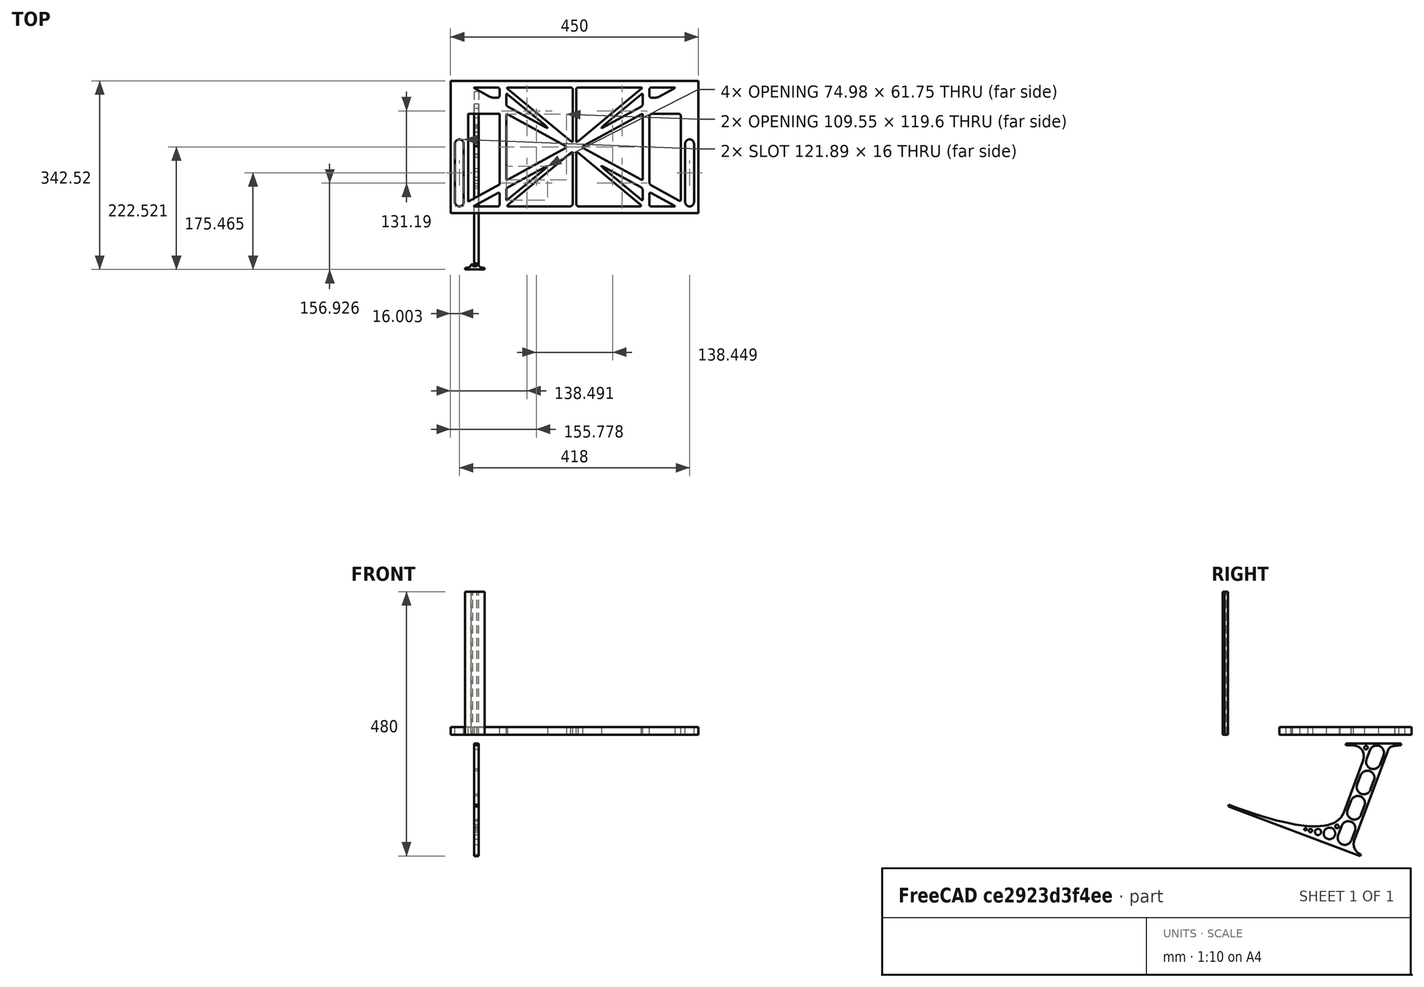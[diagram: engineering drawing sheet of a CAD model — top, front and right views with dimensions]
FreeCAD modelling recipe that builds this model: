
FCSTD DOCUMENT  (FreeCAD 0.19R0.19.2)
Label: laptopStand146FCStd
License: All rights reserved
LicenseURL: http://en.wikipedia.org/wiki/All_rights_reserved
objects: Sketcher::SketchObject×4, Part::Extrusion×3
note: 7 computed .brp shape members not serialized (recipe doc carries the construction recipe); baked Part::Feature solids carry a one-line shape summary decoded from their .brp

FEATURE [Sketcher::SketchObject] Sketch
  FullyConstrained = false
  sketch-geometry (349):
    g0: LineSegment StartX=-10.9272 StartY=-82.7794 StartZ=0 EndX=46.0728 EndY=-51.4823 EndZ=0
    g1: LineSegment StartX=-10.9272 StartY=76.4095 StartZ=0 EndX=-10.9272 EndY=-82.7794 EndZ=0
    g2: LineSegment StartX=46.0728 StartY=76.4095 StartZ=0 EndX=46.0728 EndY=-51.4823 EndZ=0
    g3: LineSegment StartX=-42.9272 StartY=136.221 StartZ=0 EndX=-42.9272 EndY=-103.779 EndZ=0
    g4: LineSegment StartX=407.073 StartY=136.221 StartZ=0 EndX=407.073 EndY=-103.779 EndZ=0
    g5: ArcOfCircle CenterX=-26.9272 CenterY=-83.7794 CenterZ=0 NormalX=0 NormalY=0 NormalZ=1 AngleXU=0 Radius=8 StartAngle=3.14159 EndAngle=6.28319
    g6: ArcOfCircle CenterX=391.073 CenterY=22.1087 CenterZ=0 NormalX=0 NormalY=0 NormalZ=1 AngleXU=0 Radius=8 StartAngle=-4.4e-15 EndAngle=3.14159
    g7: LineSegment StartX=399.073 StartY=22.1087 StartZ=0 EndX=399.073 EndY=-83.7794 EndZ=0
    g8: LineSegment StartX=383.073 StartY=22.1087 StartZ=0 EndX=383.073 EndY=-83.7794 EndZ=0
    g9: ArcOfCircle CenterX=391.073 CenterY=-83.7794 CenterZ=0 NormalX=0 NormalY=0 NormalZ=1 AngleXU=0 Radius=8 StartAngle=3.14159 EndAngle=6.28319
    g10: Circle CenterX=175.022 CenterY=27.0628 CenterZ=0 NormalX=0 NormalY=0 NormalZ=1 AngleXU=0 Radius=1
    g11: Circle CenterX=179.022 CenterY=24.8665 CenterZ=0 NormalX=0 NormalY=0 NormalZ=1 AngleXU=0 Radius=1
    g12: Circle CenterX=179.022 CenterY=27.0628 CenterZ=0 NormalX=0 NormalY=0 NormalZ=1 AngleXU=0 Radius=1
    g13: BSplineCurve PolesCount=3 KnotsCount=2 Degree=2 IsPeriodic=0
    g14: GeomPoint X=175.022 Y=27.0628 Z=0
    g15: GeomPoint X=179.022 Y=27.0628 Z=0
    g16: Circle CenterX=189.124 CenterY=27.0628 CenterZ=0 NormalX=0 NormalY=0 NormalZ=1 AngleXU=0 Radius=1
    g17: Circle CenterX=185.124 CenterY=24.8665 CenterZ=0 NormalX=0 NormalY=0 NormalZ=1 AngleXU=0 Radius=1
    g18: Circle CenterX=185.124 CenterY=27.0628 CenterZ=0 NormalX=0 NormalY=0 NormalZ=1 AngleXU=0 Radius=1
    g19: BSplineCurve PolesCount=3 KnotsCount=2 Degree=2 IsPeriodic=0
    g20: GeomPoint X=189.124 Y=27.0628 Z=0
    g21: GeomPoint X=185.124 Y=27.0628 Z=0
    g22: Circle CenterX=175.022 CenterY=5.37834 CenterZ=0 NormalX=0 NormalY=0 NormalZ=1 AngleXU=0 Radius=1
    g23: Circle CenterX=179.022 CenterY=7.57463 CenterZ=0 NormalX=0 NormalY=0 NormalZ=1 AngleXU=0 Radius=1
    g24: Circle CenterX=179.022 CenterY=5.34704 CenterZ=0 NormalX=0 NormalY=0 NormalZ=1 AngleXU=0 Radius=1
    g25: BSplineCurve PolesCount=3 KnotsCount=2 Degree=2 IsPeriodic=0
    g26: GeomPoint X=175.022 Y=5.37834 Z=0
    g27: GeomPoint X=179.022 Y=5.34704 Z=0
    g28: Circle CenterX=189.124 CenterY=5.37834 CenterZ=0 NormalX=0 NormalY=0 NormalZ=1 AngleXU=0 Radius=1
    g29: Circle CenterX=185.124 CenterY=7.57463 CenterZ=0 NormalX=0 NormalY=0 NormalZ=1 AngleXU=0 Radius=1
    g30: Circle CenterX=185.124 CenterY=5.34704 CenterZ=0 NormalX=0 NormalY=0 NormalZ=1 AngleXU=0 Radius=1
    g31: BSplineCurve PolesCount=3 KnotsCount=2 Degree=2 IsPeriodic=0
    g32: GeomPoint X=189.124 Y=5.37834 Z=0
    g33: GeomPoint X=185.124 Y=5.34704 Z=0
    g34: Circle CenterX=165.871 CenterY=18.1458 CenterZ=0 NormalX=0 NormalY=0 NormalZ=1 AngleXU=0 Radius=1
    g35: Circle CenterX=169.377 CenterY=16.2206 CenterZ=0 NormalX=0 NormalY=0 NormalZ=1 AngleXU=0 Radius=1
    g36: Circle CenterX=165.871 CenterY=14.2954 CenterZ=0 NormalX=0 NormalY=0 NormalZ=1 AngleXU=0 Radius=1
    g37: BSplineCurve PolesCount=3 KnotsCount=2 Degree=2 IsPeriodic=0
    g38: GeomPoint X=165.871 Y=18.1458 Z=0
    g39: GeomPoint X=165.871 Y=14.2954 Z=0
    g40: Circle CenterX=198.275 CenterY=18.1458 CenterZ=0 NormalX=0 NormalY=0 NormalZ=1 AngleXU=0 Radius=1
    g41: Circle CenterX=194.768 CenterY=16.2206 CenterZ=0 NormalX=0 NormalY=0 NormalZ=1 AngleXU=0 Radius=1
    g42: Circle CenterX=198.275 CenterY=14.2954 CenterZ=0 NormalX=0 NormalY=0 NormalZ=1 AngleXU=0 Radius=1
    g43: BSplineCurve PolesCount=3 KnotsCount=2 Degree=2 IsPeriodic=0
    g44: GeomPoint X=198.275 Y=18.1458 Z=0
    g45: GeomPoint X=198.275 Y=14.2954 Z=0
    g46: LineSegment StartX=407.073 StartY=-103.779 StartZ=0 EndX=-42.9272 EndY=-103.779 EndZ=0
    g47: LineSegment StartX=407.073 StartY=136.221 StartZ=0 EndX=-42.9272 EndY=136.221 EndZ=0
    g48: LineSegment StartX=46.0728 StartY=76.4095 StartZ=0 EndX=-10.9272 EndY=76.4095 EndZ=0
    g49: Circle CenterX=125.607 CenterY=54.1951 CenterZ=0 NormalX=0 NormalY=0 NormalZ=1 AngleXU=0 Radius=1
    g50: Circle CenterX=139.632 CenterY=46.4944 CenterZ=0 NormalX=0 NormalY=0 NormalZ=1 AngleXU=0 Radius=1
    g51: Circle CenterX=127.326 CenterY=56.7187 CenterZ=0 NormalX=0 NormalY=0 NormalZ=1 AngleXU=0 Radius=1
    g52: BSplineCurve PolesCount=3 KnotsCount=2 Degree=2 IsPeriodic=0
    g53: GeomPoint X=125.607 Y=54.1951 Z=0
    g54: GeomPoint X=127.326 Y=56.7187 Z=0
    g55: Circle CenterX=236.821 CenterY=56.7187 CenterZ=0 NormalX=0 NormalY=0 NormalZ=1 AngleXU=0 Radius=1
    g56: Circle CenterX=224.513 CenterY=46.4944 CenterZ=0 NormalX=0 NormalY=0 NormalZ=1 AngleXU=0 Radius=1
    g57: Circle CenterX=238.538 CenterY=54.1951 CenterZ=0 NormalX=0 NormalY=0 NormalZ=1 AngleXU=0 Radius=1
    g58: BSplineCurve PolesCount=3 KnotsCount=2 Degree=2 IsPeriodic=0
    g59: GeomPoint X=236.821 Y=56.7187 Z=0
    g60: GeomPoint X=238.538 Y=54.1951 Z=0
    g61: Circle CenterX=238.538 CenterY=-21.7539 CenterZ=0 NormalX=0 NormalY=0 NormalZ=1 AngleXU=0 Radius=1
    g62: Circle CenterX=224.513 CenterY=-14.0532 CenterZ=0 NormalX=0 NormalY=0 NormalZ=1 AngleXU=0 Radius=1
    g63: Circle CenterX=236.821 CenterY=-24.2775 CenterZ=0 NormalX=0 NormalY=0 NormalZ=1 AngleXU=0 Radius=1
    g64: BSplineCurve PolesCount=3 KnotsCount=2 Degree=2 IsPeriodic=0
    g65: GeomPoint X=238.538 Y=-21.7539 Z=0
    g66: GeomPoint X=236.821 Y=-24.2775 Z=0
    g67: Circle CenterX=125.607 CenterY=-21.7539 CenterZ=0 NormalX=0 NormalY=0 NormalZ=1 AngleXU=0 Radius=1
    g68: Circle CenterX=139.632 CenterY=-14.0532 CenterZ=0 NormalX=0 NormalY=0 NormalZ=1 AngleXU=0 Radius=1
    g69: Circle CenterX=127.325 CenterY=-24.2775 CenterZ=0 NormalX=0 NormalY=0 NormalZ=1 AngleXU=0 Radius=1
    g70: BSplineCurve PolesCount=3 KnotsCount=2 Degree=2 IsPeriodic=0
    g71: GeomPoint X=125.607 Y=-21.7539 Z=0
    g72: GeomPoint X=127.325 Y=-24.2775 Z=0
    g73: Circle CenterX=302.996 CenterY=111.695 CenterZ=0 NormalX=0 NormalY=0 NormalZ=1 AngleXU=0 Radius=1
    g74: Circle CenterX=306.073 CenterY=114.251 CenterZ=0 NormalX=0 NormalY=0 NormalZ=1 AngleXU=0 Radius=1
    g75: Circle CenterX=306.073 CenterY=110.251 CenterZ=0 NormalX=0 NormalY=0 NormalZ=1 AngleXU=0 Radius=1
    g76: BSplineCurve PolesCount=3 KnotsCount=2 Degree=2 IsPeriodic=0
    g77: GeomPoint X=302.996 Y=111.695 Z=0
    g78: GeomPoint X=306.073 Y=110.251 Z=0
    g79: Circle CenterX=306.073 CenterY=95.2763 CenterZ=0 NormalX=0 NormalY=0 NormalZ=1 AngleXU=0 Radius=1
    g80: Circle CenterX=306.073 CenterY=91.2763 CenterZ=0 NormalX=0 NormalY=0 NormalZ=1 AngleXU=0 Radius=1
    g81: Circle CenterX=302.567 CenterY=89.3511 CenterZ=0 NormalX=0 NormalY=0 NormalZ=1 AngleXU=0 Radius=1
    g82: BSplineCurve PolesCount=3 KnotsCount=2 Degree=2 IsPeriodic=0
    g83: GeomPoint X=306.073 Y=95.2763 Z=0
    g84: GeomPoint X=302.567 Y=89.3511 Z=0
    g85: LineSegment StartX=306.073 StartY=110.251 StartZ=0 EndX=306.073 EndY=95.2763 EndZ=0
    g86: LineSegment StartX=302.996 StartY=111.695 StartZ=0 EndX=236.821 EndY=56.7187 EndZ=0
    g87: LineSegment StartX=238.538 StartY=54.1951 StartZ=0 EndX=302.567 EndY=89.3511 EndZ=0
    g88: Circle CenterX=61.1496 CenterY=111.695 CenterZ=0 NormalX=0 NormalY=0 NormalZ=1 AngleXU=0 Radius=1
    g89: Circle CenterX=58.0728 CenterY=114.251 CenterZ=0 NormalX=0 NormalY=0 NormalZ=1 AngleXU=0 Radius=1
    g90: Circle CenterX=58.0728 CenterY=110.251 CenterZ=0 NormalX=0 NormalY=0 NormalZ=1 AngleXU=0 Radius=1
    g91: BSplineCurve PolesCount=3 KnotsCount=2 Degree=2 IsPeriodic=0
    g92: GeomPoint X=61.1496 Y=111.695 Z=0
    g93: GeomPoint X=58.0728 Y=110.251 Z=0
    g94: Circle CenterX=61.5791 CenterY=89.3511 CenterZ=0 NormalX=0 NormalY=0 NormalZ=1 AngleXU=0 Radius=1
    g95: Circle CenterX=58.0728 CenterY=91.2763 CenterZ=0 NormalX=0 NormalY=0 NormalZ=1 AngleXU=0 Radius=1
    g96: Circle CenterX=58.0728 CenterY=95.2763 CenterZ=0 NormalX=0 NormalY=0 NormalZ=1 AngleXU=0 Radius=1
    g97: BSplineCurve PolesCount=3 KnotsCount=2 Degree=2 IsPeriodic=0
    g98: GeomPoint X=61.5791 Y=89.3511 Z=0
    g99: GeomPoint X=58.0728 Y=95.2763 Z=0
    g100: LineSegment StartX=58.0728 StartY=110.251 StartZ=0 EndX=58.0728 EndY=95.2763 EndZ=0
    g101: LineSegment StartX=61.1496 StartY=111.695 StartZ=0 EndX=127.326 EndY=56.7187 EndZ=0
    g102: LineSegment StartX=125.607 StartY=54.1951 StartZ=0 EndX=61.5791 EndY=89.3511 EndZ=0
    g103: Circle CenterX=61.5791 CenterY=-56.9099 CenterZ=0 NormalX=0 NormalY=0 NormalZ=1 AngleXU=0 Radius=1
    g104: Circle CenterX=58.0728 CenterY=-58.8351 CenterZ=0 NormalX=0 NormalY=0 NormalZ=1 AngleXU=0 Radius=1
    g105: Circle CenterX=58.0728 CenterY=-62.8351 CenterZ=0 NormalX=0 NormalY=0 NormalZ=1 AngleXU=0 Radius=1
    g106: BSplineCurve PolesCount=3 KnotsCount=2 Degree=2 IsPeriodic=0
    g107: GeomPoint X=61.5791 Y=-56.9099 Z=0
    g108: GeomPoint X=58.0728 Y=-62.8351 Z=0
    g109: Circle CenterX=58.0728 CenterY=-77.8102 CenterZ=0 NormalX=0 NormalY=0 NormalZ=1 AngleXU=0 Radius=1
    g110: Circle CenterX=58.0728 CenterY=-81.8102 CenterZ=0 NormalX=0 NormalY=0 NormalZ=1 AngleXU=0 Radius=1
    g111: Circle CenterX=61.1496 CenterY=-79.2541 CenterZ=0 NormalX=0 NormalY=0 NormalZ=1 AngleXU=0 Radius=1
    g112: BSplineCurve PolesCount=3 KnotsCount=2 Degree=2 IsPeriodic=0
    g113: GeomPoint X=58.0728 Y=-77.8102 Z=0
    g114: GeomPoint X=61.1496 Y=-79.2541 Z=0
    g115: LineSegment StartX=58.0728 StartY=-62.8351 StartZ=0 EndX=58.0728 EndY=-77.8102 EndZ=0
    g116: LineSegment StartX=61.1496 StartY=-79.2541 StartZ=0 EndX=127.325 EndY=-24.2775 EndZ=0
    g117: LineSegment StartX=125.607 StartY=-21.7539 StartZ=0 EndX=61.5791 EndY=-56.9099 EndZ=0
    g118: Circle CenterX=302.567 CenterY=-56.9099 CenterZ=0 NormalX=0 NormalY=0 NormalZ=1 AngleXU=0 Radius=1
    g119: Circle CenterX=306.073 CenterY=-58.8351 CenterZ=0 NormalX=0 NormalY=0 NormalZ=1 AngleXU=0 Radius=1
    g120: Circle CenterX=306.073 CenterY=-62.8351 CenterZ=0 NormalX=0 NormalY=0 NormalZ=1 AngleXU=0 Radius=1
    g121: BSplineCurve PolesCount=3 KnotsCount=2 Degree=2 IsPeriodic=0
    g122: GeomPoint X=302.567 Y=-56.9099 Z=0
    g123: GeomPoint X=306.073 Y=-62.8351 Z=0
    g124: Circle CenterX=302.996 CenterY=-79.2541 CenterZ=0 NormalX=0 NormalY=0 NormalZ=1 AngleXU=0 Radius=1
    g125: Circle CenterX=306.073 CenterY=-81.8102 CenterZ=0 NormalX=0 NormalY=0 NormalZ=1 AngleXU=0 Radius=1
    g126: Circle CenterX=306.073 CenterY=-77.8102 CenterZ=0 NormalX=0 NormalY=0 NormalZ=1 AngleXU=0 Radius=1
    g127: BSplineCurve PolesCount=3 KnotsCount=2 Degree=2 IsPeriodic=0
    g128: GeomPoint X=302.996 Y=-79.2541 Z=0
    g129: GeomPoint X=306.073 Y=-77.8102 Z=0
    g130: LineSegment StartX=306.073 StartY=-62.8351 StartZ=0 EndX=306.073 EndY=-77.8102 EndZ=0
    g131: LineSegment StartX=302.996 StartY=-79.2541 StartZ=0 EndX=236.821 EndY=-24.2775 EndZ=0
    g132: LineSegment StartX=238.538 StartY=-21.7539 StartZ=0 EndX=302.567 EndY=-56.9099 EndZ=0
    g133: Circle CenterX=61.6457 CenterY=-88.8112 CenterZ=0 NormalX=0 NormalY=0 NormalZ=1 AngleXU=0 Radius=1
    g134: Circle CenterX=58.0728 CenterY=-91.7794 CenterZ=0 NormalX=0 NormalY=0 NormalZ=1 AngleXU=0 Radius=1
    g135: Circle CenterX=63.9135 CenterY=-91.7794 CenterZ=0 NormalX=0 NormalY=0 NormalZ=1 AngleXU=0 Radius=1
    g136: BSplineCurve PolesCount=3 KnotsCount=2 Degree=2 IsPeriodic=0
    g137: GeomPoint X=61.6457 Y=-88.8112 Z=0
    g138: GeomPoint X=63.9135 Y=-91.7794 Z=0
    g139: Circle CenterX=179.022 CenterY=-85.8163 CenterZ=0 NormalX=0 NormalY=0 NormalZ=1 AngleXU=0 Radius=1
    g140: Circle CenterX=179.022 CenterY=-91.7794 CenterZ=0 NormalX=0 NormalY=0 NormalZ=1 AngleXU=0 Radius=1
    g141: Circle CenterX=171.895 CenterY=-91.7794 CenterZ=0 NormalX=0 NormalY=0 NormalZ=1 AngleXU=0 Radius=1
    g142: BSplineCurve PolesCount=3 KnotsCount=2 Degree=2 IsPeriodic=0
    g143: GeomPoint X=179.022 Y=-85.8163 Z=0
    g144: GeomPoint X=171.895 Y=-91.7794 Z=0
    g145: Circle CenterX=185.124 CenterY=-86.2028 CenterZ=0 NormalX=0 NormalY=0 NormalZ=1 AngleXU=0 Radius=1
    g146: Circle CenterX=185.124 CenterY=-91.7794 CenterZ=0 NormalX=0 NormalY=0 NormalZ=1 AngleXU=0 Radius=1
    g147: Circle CenterX=191.747 CenterY=-91.7794 CenterZ=0 NormalX=0 NormalY=0 NormalZ=1 AngleXU=0 Radius=1
    g148: BSplineCurve PolesCount=3 KnotsCount=2 Degree=2 IsPeriodic=0
    g149: GeomPoint X=185.124 Y=-86.2028 Z=0
    g150: GeomPoint X=191.747 Y=-91.7794 Z=0
    g151: Circle CenterX=299.888 CenterY=-86.6413 CenterZ=0 NormalX=0 NormalY=0 NormalZ=1 AngleXU=0 Radius=1
    g152: Circle CenterX=306.073 CenterY=-91.7794 CenterZ=0 NormalX=0 NormalY=0 NormalZ=1 AngleXU=0 Radius=1
    g153: Circle CenterX=298.776 CenterY=-91.7794 CenterZ=0 NormalX=0 NormalY=0 NormalZ=1 AngleXU=0 Radius=1
    g154: BSplineCurve PolesCount=3 KnotsCount=2 Degree=2 IsPeriodic=0
    g155: GeomPoint X=299.888 Y=-86.6413 Z=0
    g156: GeomPoint X=298.776 Y=-91.7794 Z=0
    g157: LineSegment StartX=189.124 StartY=5.37834 StartZ=0 EndX=299.888 EndY=-86.6413 EndZ=0
    g158: LineSegment StartX=298.776 StartY=-91.7794 StartZ=0 EndX=191.747 EndY=-91.7794 EndZ=0
    g159: LineSegment StartX=185.124 StartY=-86.2028 StartZ=0 EndX=185.124 EndY=5.34704 EndZ=0
    g160: LineSegment StartX=179.022 StartY=5.34704 StartZ=0 EndX=179.022 EndY=-85.8163 EndZ=0
    g161: LineSegment StartX=171.895 StartY=-91.7794 StartZ=0 EndX=63.9135 EndY=-91.7794 EndZ=0
    g162: LineSegment StartX=61.6457 StartY=-88.8112 StartZ=0 EndX=175.022 EndY=5.37834 EndZ=0
    g163: Circle CenterX=302.073 CenterY=124.221 CenterZ=0 NormalX=0 NormalY=0 NormalZ=1 AngleXU=0 Radius=1
    g164: Circle CenterX=306.073 CenterY=124.221 CenterZ=0 NormalX=0 NormalY=0 NormalZ=1 AngleXU=0 Radius=1
    g165: Circle CenterX=302.996 CenterY=121.665 CenterZ=0 NormalX=0 NormalY=0 NormalZ=1 AngleXU=0 Radius=1
    g166: BSplineCurve PolesCount=3 KnotsCount=2 Degree=2 IsPeriodic=0
    g167: GeomPoint X=302.073 Y=124.221 Z=0
    g168: GeomPoint X=302.996 Y=121.665 Z=0
    g169: Circle CenterX=189.124 CenterY=124.221 CenterZ=0 NormalX=0 NormalY=0 NormalZ=1 AngleXU=0 Radius=1
    g170: Circle CenterX=185.124 CenterY=124.221 CenterZ=0 NormalX=0 NormalY=0 NormalZ=1 AngleXU=0 Radius=1
    g171: Circle CenterX=185.124 CenterY=120.221 CenterZ=0 NormalX=0 NormalY=0 NormalZ=1 AngleXU=0 Radius=1
    g172: BSplineCurve PolesCount=3 KnotsCount=2 Degree=2 IsPeriodic=0
    g173: GeomPoint X=189.124 Y=124.221 Z=0
    g174: GeomPoint X=185.124 Y=120.221 Z=0
    g175: Circle CenterX=175.022 CenterY=124.221 CenterZ=0 NormalX=0 NormalY=0 NormalZ=1 AngleXU=0 Radius=1
    g176: Circle CenterX=179.022 CenterY=124.221 CenterZ=0 NormalX=0 NormalY=0 NormalZ=1 AngleXU=0 Radius=1
    g177: Circle CenterX=179.022 CenterY=120.221 CenterZ=0 NormalX=0 NormalY=0 NormalZ=1 AngleXU=0 Radius=1
    g178: BSplineCurve PolesCount=3 KnotsCount=2 Degree=2 IsPeriodic=0
    g179: GeomPoint X=175.022 Y=124.221 Z=0
    g180: GeomPoint X=179.022 Y=120.221 Z=0
    g181: Circle CenterX=62.0728 CenterY=124.221 CenterZ=0 NormalX=0 NormalY=0 NormalZ=1 AngleXU=0 Radius=1
    g182: Circle CenterX=58.0728 CenterY=124.221 CenterZ=0 NormalX=0 NormalY=0 NormalZ=1 AngleXU=0 Radius=1
    g183: Circle CenterX=61.1496 CenterY=121.665 CenterZ=0 NormalX=0 NormalY=0 NormalZ=1 AngleXU=0 Radius=1
    g184: BSplineCurve PolesCount=3 KnotsCount=2 Degree=2 IsPeriodic=0
    g185: GeomPoint X=62.0728 Y=124.221 Z=0
    g186: GeomPoint X=61.1496 Y=121.665 Z=0
    g187: LineSegment StartX=62.0728 StartY=124.221 StartZ=0 EndX=175.022 EndY=124.221 EndZ=0
    g188: LineSegment StartX=179.022 StartY=120.221 StartZ=0 EndX=179.022 EndY=27.0628 EndZ=0
    g189: LineSegment StartX=185.124 StartY=27.0628 StartZ=0 EndX=185.124 EndY=120.221 EndZ=0
    g190: LineSegment StartX=189.124 StartY=124.221 StartZ=0 EndX=302.073 EndY=124.221 EndZ=0
    g191: LineSegment StartX=302.996 StartY=121.665 StartZ=0 EndX=189.124 EndY=27.0628 EndZ=0
    g192: LineSegment StartX=175.022 StartY=27.0628 StartZ=0 EndX=61.1496 EndY=121.665 EndZ=0
    g193: Circle CenterX=61.5791 CenterY=75.4095 CenterZ=0 NormalX=0 NormalY=0 NormalZ=1 AngleXU=0 Radius=1
    g194: Circle CenterX=58.0728 CenterY=77.3346 CenterZ=0 NormalX=0 NormalY=0 NormalZ=1 AngleXU=0 Radius=1
    g195: Circle CenterX=58.0728 CenterY=73.3346 CenterZ=0 NormalX=0 NormalY=0 NormalZ=1 AngleXU=0 Radius=1
    g196: BSplineCurve PolesCount=3 KnotsCount=2 Degree=2 IsPeriodic=0
    g197: GeomPoint X=61.5791 Y=75.4095 Z=0
    g198: GeomPoint X=58.0728 Y=73.3346 Z=0
    g199: Circle CenterX=58.0728 CenterY=-40.8935 CenterZ=0 NormalX=0 NormalY=0 NormalZ=1 AngleXU=0 Radius=1
    g200: Circle CenterX=58.0728 CenterY=-44.8935 CenterZ=0 NormalX=0 NormalY=0 NormalZ=1 AngleXU=0 Radius=1
    g201: Circle CenterX=61.5791 CenterY=-42.9683 CenterZ=0 NormalX=0 NormalY=0 NormalZ=1 AngleXU=0 Radius=1
    g202: BSplineCurve PolesCount=3 KnotsCount=2 Degree=2 IsPeriodic=0
    g203: GeomPoint X=58.0728 Y=-40.8935 Z=0
    g204: GeomPoint X=61.5791 Y=-42.9683 Z=0
    g205: LineSegment StartX=61.5791 StartY=-42.9683 StartZ=0 EndX=165.871 EndY=14.2954 EndZ=0
    g206: LineSegment StartX=165.871 StartY=18.1458 StartZ=0 EndX=61.5791 EndY=75.4095 EndZ=0
    g207: LineSegment StartX=58.0728 StartY=73.3346 StartZ=0 EndX=58.0728 EndY=-40.8935 EndZ=0
    g208: Circle CenterX=302.567 CenterY=-42.9683 CenterZ=0 NormalX=0 NormalY=0 NormalZ=1 AngleXU=0 Radius=1
    g209: Circle CenterX=306.073 CenterY=-44.8935 CenterZ=0 NormalX=0 NormalY=0 NormalZ=1 AngleXU=0 Radius=1
    g210: Circle CenterX=306.073 CenterY=-40.8935 CenterZ=0 NormalX=0 NormalY=0 NormalZ=1 AngleXU=0 Radius=1
    g211: BSplineCurve PolesCount=3 KnotsCount=2 Degree=2 IsPeriodic=0
    g212: GeomPoint X=302.567 Y=-42.9683 Z=0
    g213: GeomPoint X=306.073 Y=-40.8935 Z=0
    g214: Circle CenterX=306.073 CenterY=73.3346 CenterZ=0 NormalX=0 NormalY=0 NormalZ=1 AngleXU=0 Radius=1
    g215: Circle CenterX=306.073 CenterY=77.3346 CenterZ=0 NormalX=0 NormalY=0 NormalZ=1 AngleXU=0 Radius=1
    g216: Circle CenterX=302.567 CenterY=75.4095 CenterZ=0 NormalX=0 NormalY=0 NormalZ=1 AngleXU=0 Radius=1
    g217: BSplineCurve PolesCount=3 KnotsCount=2 Degree=2 IsPeriodic=0
    g218: GeomPoint X=306.073 Y=73.3346 Z=0
    g219: GeomPoint X=302.567 Y=75.4095 Z=0
    g220: LineSegment StartX=302.567 StartY=-42.9683 StartZ=0 EndX=198.275 EndY=14.2954 EndZ=0
    g221: LineSegment StartX=198.275 StartY=18.1458 StartZ=0 EndX=302.567 EndY=75.4095 EndZ=0
    g222: LineSegment StartX=306.073 StartY=73.3346 StartZ=0 EndX=306.073 EndY=-40.8935 EndZ=0
    g223: LineSegment StartX=322.073 StartY=105.865 StartZ=0 EndX=328.643 EndY=105.865 EndZ=0
    g224: LineSegment StartX=318.073 StartY=120.221 StartZ=0 EndX=318.073 EndY=109.865 EndZ=0
    g225: LineSegment StartX=336.157 StartY=107.779 StartZ=0 EndX=362.567 EndY=122.294 EndZ=0
    g226: Circle CenterX=362.073 CenterY=124.221 CenterZ=0 NormalX=0 NormalY=0 NormalZ=1 AngleXU=0 Radius=1
    g227: Circle CenterX=366.073 CenterY=124.221 CenterZ=0 NormalX=0 NormalY=0 NormalZ=1 AngleXU=0 Radius=1
    g228: Circle CenterX=362.567 CenterY=122.294 CenterZ=0 NormalX=0 NormalY=0 NormalZ=1 AngleXU=0 Radius=1
    g229: BSplineCurve PolesCount=3 KnotsCount=2 Degree=2 IsPeriodic=0
    g230: GeomPoint X=362.073 Y=124.221 Z=0
    g231: GeomPoint X=362.567 Y=122.294 Z=0
    g232: Circle CenterX=322.073 CenterY=124.221 CenterZ=0 NormalX=0 NormalY=0 NormalZ=1 AngleXU=0 Radius=1
    g233: Circle CenterX=318.073 CenterY=124.221 CenterZ=0 NormalX=0 NormalY=0 NormalZ=1 AngleXU=0 Radius=1
    g234: Circle CenterX=318.073 CenterY=120.221 CenterZ=0 NormalX=0 NormalY=0 NormalZ=1 AngleXU=0 Radius=1
    g235: BSplineCurve PolesCount=3 KnotsCount=2 Degree=2 IsPeriodic=0
    g236: GeomPoint X=322.073 Y=124.221 Z=0
    g237: GeomPoint X=318.073 Y=120.221 Z=0
    g238: Circle CenterX=322.073 CenterY=105.865 CenterZ=0 NormalX=0 NormalY=0 NormalZ=1 AngleXU=0 Radius=1
    g239: Circle CenterX=318.073 CenterY=105.865 CenterZ=0 NormalX=0 NormalY=0 NormalZ=1 AngleXU=0 Radius=1
    g240: Circle CenterX=318.073 CenterY=109.865 CenterZ=0 NormalX=0 NormalY=0 NormalZ=1 AngleXU=0 Radius=1
    g241: BSplineCurve PolesCount=3 KnotsCount=2 Degree=2 IsPeriodic=0
    g242: GeomPoint X=322.073 Y=105.865 Z=0
    g243: GeomPoint X=318.073 Y=109.865 Z=0
    g244: Circle CenterX=336.157 CenterY=107.779 CenterZ=0 NormalX=0 NormalY=0 NormalZ=1 AngleXU=0 Radius=1
    g245: Circle CenterX=332.651 CenterY=105.853 CenterZ=0 NormalX=0 NormalY=0 NormalZ=1 AngleXU=0 Radius=1
    g246: Circle CenterX=328.643 CenterY=105.865 CenterZ=0 NormalX=0 NormalY=0 NormalZ=1 AngleXU=0 Radius=1
    g247: BSplineCurve PolesCount=3 KnotsCount=2 Degree=2 IsPeriodic=0
    g248: GeomPoint X=336.157 Y=107.779 Z=0
    g249: GeomPoint X=328.643 Y=105.865 Z=0
    g250: LineSegment StartX=322.073 StartY=124.221 StartZ=0 EndX=362.073 EndY=124.221 EndZ=0
    g251: Circle CenterX=371.567 CenterY=-80.8644 CenterZ=0 NormalX=0 NormalY=0 NormalZ=1 AngleXU=0 Radius=1
    g252: Circle CenterX=375.073 CenterY=-82.7896 CenterZ=0 NormalX=0 NormalY=0 NormalZ=1 AngleXU=0 Radius=1
    g253: Circle CenterX=375.073 CenterY=-78.7896 CenterZ=0 NormalX=0 NormalY=0 NormalZ=1 AngleXU=0 Radius=1
    g254: BSplineCurve PolesCount=3 KnotsCount=2 Degree=2 IsPeriodic=0
    g255: GeomPoint X=371.567 Y=-80.8644 Z=0
    g256: GeomPoint X=375.073 Y=-78.7896 Z=0
    g257: Circle CenterX=321.579 CenterY=-53.4075 CenterZ=0 NormalX=0 NormalY=0 NormalZ=1 AngleXU=0 Radius=1
    g258: Circle CenterX=318.073 CenterY=-51.4823 CenterZ=0 NormalX=0 NormalY=0 NormalZ=1 AngleXU=0 Radius=1
    g259: Circle CenterX=318.073 CenterY=-47.4805 CenterZ=0 NormalX=0 NormalY=0 NormalZ=1 AngleXU=0 Radius=1
    g260: BSplineCurve PolesCount=3 KnotsCount=2 Degree=2 IsPeriodic=0
    g261: GeomPoint X=321.579 Y=-53.4075 Z=0
    g262: GeomPoint X=318.073 Y=-47.4805 Z=0
    g263: LineSegment StartX=371.567 StartY=-80.8644 StartZ=0 EndX=321.579 EndY=-53.4075 EndZ=0
    g264: Circle CenterX=321.579 CenterY=-67.3492 CenterZ=0 NormalX=0 NormalY=0 NormalZ=1 AngleXU=0 Radius=1
    g265: Circle CenterX=318.073 CenterY=-65.424 CenterZ=0 NormalX=0 NormalY=0 NormalZ=1 AngleXU=0 Radius=1
    g266: Circle CenterX=318.073 CenterY=-69.424 CenterZ=0 NormalX=0 NormalY=0 NormalZ=1 AngleXU=0 Radius=1
    g267: BSplineCurve PolesCount=3 KnotsCount=2 Degree=2 IsPeriodic=0
    g268: GeomPoint X=321.579 Y=-67.3492 Z=0
    g269: GeomPoint X=318.073 Y=-69.424 Z=0
    g270: Circle CenterX=362.567 CenterY=-89.8542 CenterZ=0 NormalX=0 NormalY=0 NormalZ=1 AngleXU=0 Radius=1
    g271: Circle CenterX=366.073 CenterY=-91.7794 CenterZ=0 NormalX=0 NormalY=0 NormalZ=1 AngleXU=0 Radius=1
    g272: Circle CenterX=362.073 CenterY=-91.7794 CenterZ=0 NormalX=0 NormalY=0 NormalZ=1 AngleXU=0 Radius=1
    g273: BSplineCurve PolesCount=3 KnotsCount=2 Degree=2 IsPeriodic=0
    g274: GeomPoint X=362.567 Y=-89.8542 Z=0
    g275: GeomPoint X=362.073 Y=-91.7794 Z=0
    g276: Circle CenterX=322.073 CenterY=-91.7794 CenterZ=0 NormalX=0 NormalY=0 NormalZ=1 AngleXU=0 Radius=1
    g277: Circle CenterX=318.073 CenterY=-91.7794 CenterZ=0 NormalX=0 NormalY=0 NormalZ=1 AngleXU=0 Radius=1
    g278: Circle CenterX=318.073 CenterY=-87.7794 CenterZ=0 NormalX=0 NormalY=0 NormalZ=1 AngleXU=0 Radius=1
    g279: BSplineCurve PolesCount=3 KnotsCount=2 Degree=2 IsPeriodic=0
    g280: GeomPoint X=322.073 Y=-91.7794 Z=0
    g281: GeomPoint X=318.073 Y=-87.7794 Z=0
    g282: LineSegment StartX=362.567 StartY=-89.8542 StartZ=0 EndX=321.579 EndY=-67.3492 EndZ=0
    g283: LineSegment StartX=318.073 StartY=-69.424 StartZ=0 EndX=318.073 EndY=-87.7794 EndZ=0
    g284: LineSegment StartX=322.073 StartY=-91.7794 StartZ=0 EndX=362.073 EndY=-91.7794 EndZ=0
    g285: Circle CenterX=2.07281 CenterY=124.221 CenterZ=0 NormalX=0 NormalY=0 NormalZ=1 AngleXU=0 Radius=1
    g286: Circle CenterX=1.57905 CenterY=122.295 CenterZ=0 NormalX=0 NormalY=0 NormalZ=1 AngleXU=0 Radius=1
    g287: BSplineCurve PolesCount=3 KnotsCount=2 Degree=2 IsPeriodic=0
    g288: GeomPoint X=2.07281 Y=124.221 Z=0
    g289: GeomPoint X=1.57905 Y=122.295 Z=0
    g290: Circle CenterX=42.0728 CenterY=124.221 CenterZ=0 NormalX=0 NormalY=0 NormalZ=1 AngleXU=0 Radius=1
    g291: Circle CenterX=46.0728 CenterY=124.221 CenterZ=0 NormalX=0 NormalY=0 NormalZ=1 AngleXU=0 Radius=1
    g292: Circle CenterX=46.0728 CenterY=120.221 CenterZ=0 NormalX=0 NormalY=0 NormalZ=1 AngleXU=0 Radius=1
    g293: BSplineCurve PolesCount=3 KnotsCount=2 Degree=2 IsPeriodic=0
    g294: GeomPoint X=42.0728 Y=124.221 Z=0
    g295: GeomPoint X=46.0728 Y=120.221 Z=0
    g296: Circle CenterX=46.0728 CenterY=109.865 CenterZ=0 NormalX=0 NormalY=0 NormalZ=1 AngleXU=0 Radius=1
    g297: Circle CenterX=46.0728 CenterY=105.865 CenterZ=0 NormalX=0 NormalY=0 NormalZ=1 AngleXU=0 Radius=1
    g298: Circle CenterX=42.0728 CenterY=105.865 CenterZ=0 NormalX=0 NormalY=0 NormalZ=1 AngleXU=0 Radius=1
    g299: BSplineCurve PolesCount=3 KnotsCount=2 Degree=2 IsPeriodic=0
    g300: GeomPoint X=46.0728 Y=109.865 Z=0
    g301: GeomPoint X=42.0728 Y=105.865 Z=0
    g302: Circle CenterX=35.5028 CenterY=105.865 CenterZ=0 NormalX=0 NormalY=0 NormalZ=1 AngleXU=0 Radius=1
    g303: Circle CenterX=31.5028 CenterY=105.865 CenterZ=0 NormalX=0 NormalY=0 NormalZ=1 AngleXU=0 Radius=1
    g304: Circle CenterX=27.9965 CenterY=107.79 CenterZ=0 NormalX=0 NormalY=0 NormalZ=1 AngleXU=0 Radius=1
    g305: BSplineCurve PolesCount=3 KnotsCount=2 Degree=2 IsPeriodic=0
    g306: GeomPoint X=35.5028 Y=105.865 Z=0
    g307: GeomPoint X=27.9965 Y=107.79 Z=0
    g308: LineSegment StartX=2.07281 StartY=124.221 StartZ=0 EndX=42.0728 EndY=124.221 EndZ=0
    g309: LineSegment StartX=46.0728 StartY=120.221 StartZ=0 EndX=46.0728 EndY=109.865 EndZ=0
    g310: LineSegment StartX=42.0728 StartY=105.865 StartZ=0 EndX=35.5028 EndY=105.865 EndZ=0
    g311: LineSegment StartX=27.9965 StartY=107.79 StartZ=0 EndX=1.57905 EndY=122.295 EndZ=0
    g312: Circle CenterX=42.5666 CenterY=-67.3492 CenterZ=0 NormalX=0 NormalY=0 NormalZ=1 AngleXU=0 Radius=1
    g313: Circle CenterX=46.0728 CenterY=-65.424 CenterZ=0 NormalX=0 NormalY=0 NormalZ=1 AngleXU=0 Radius=1
    g314: Circle CenterX=46.0728 CenterY=-69.424 CenterZ=0 NormalX=0 NormalY=0 NormalZ=1 AngleXU=0 Radius=1
    g315: BSplineCurve PolesCount=3 KnotsCount=2 Degree=2 IsPeriodic=0
    g316: GeomPoint X=42.5666 Y=-67.3492 Z=0
    g317: GeomPoint X=46.0728 Y=-69.424 Z=0
    g318: Circle CenterX=46.0728 CenterY=-87.7794 CenterZ=0 NormalX=0 NormalY=0 NormalZ=1 AngleXU=0 Radius=1
    g319: Circle CenterX=46.0728 CenterY=-91.7794 CenterZ=0 NormalX=0 NormalY=0 NormalZ=1 AngleXU=0 Radius=1
    g320: Circle CenterX=42.0728 CenterY=-91.7794 CenterZ=0 NormalX=0 NormalY=0 NormalZ=1 AngleXU=0 Radius=1
    g321: BSplineCurve PolesCount=3 KnotsCount=2 Degree=2 IsPeriodic=0
    g322: GeomPoint X=46.0728 Y=-87.7794 Z=0
    g323: GeomPoint X=42.0728 Y=-91.7794 Z=0
    g324: Circle CenterX=2.07281 CenterY=-91.7794 CenterZ=0 NormalX=0 NormalY=0 NormalZ=1 AngleXU=0 Radius=1
    g325: Circle CenterX=-1.92719 CenterY=-91.7794 CenterZ=0 NormalX=0 NormalY=0 NormalZ=1 AngleXU=0 Radius=1
    g326: Circle CenterX=1.57905 CenterY=-89.8542 CenterZ=0 NormalX=0 NormalY=0 NormalZ=1 AngleXU=0 Radius=1
    g327: BSplineCurve PolesCount=3 KnotsCount=2 Degree=2 IsPeriodic=0
    g328: GeomPoint X=2.07281 Y=-91.7794 Z=0
    g329: GeomPoint X=1.57905 Y=-89.8542 Z=0
    g330: LineSegment StartX=2.07281 StartY=-91.7794 StartZ=0 EndX=42.0728 EndY=-91.7794 EndZ=0
    g331: LineSegment StartX=46.0728 StartY=-87.7794 StartZ=0 EndX=46.0728 EndY=-69.424 EndZ=0
    g332: LineSegment StartX=42.5666 StartY=-67.3492 StartZ=0 EndX=1.57905 EndY=-89.8542 EndZ=0
    g333: Circle CenterX=322.073 CenterY=76.4095 CenterZ=0 NormalX=0 NormalY=0 NormalZ=1 AngleXU=0 Radius=4
    g334: BSplineCurve PolesCount=3 KnotsCount=2 Degree=2 IsPeriodic=0
    g335: GeomPoint X=318.073 Y=72.4095 Z=0
    g336: GeomPoint X=322.073 Y=76.4095 Z=0
    g337: Circle CenterX=375.073 CenterY=72.4095 CenterZ=0 NormalX=0 NormalY=0 NormalZ=1 AngleXU=0 Radius=1
    g338: Circle CenterX=375.073 CenterY=76.4095 CenterZ=0 NormalX=0 NormalY=0 NormalZ=1 AngleXU=0 Radius=1
    g339: Circle CenterX=371.073 CenterY=76.4095 CenterZ=0 NormalX=0 NormalY=0 NormalZ=1 AngleXU=0 Radius=1
    g340: BSplineCurve PolesCount=3 KnotsCount=2 Degree=2 IsPeriodic=0
    g341: GeomPoint X=375.073 Y=72.4095 Z=0
    g342: GeomPoint X=371.073 Y=76.4095 Z=0
    g343: LineSegment StartX=322.073 StartY=76.4095 StartZ=0 EndX=371.073 EndY=76.4095 EndZ=0
    g344: LineSegment StartX=318.073 StartY=72.4095 StartZ=0 EndX=318.073 EndY=-47.4805 EndZ=0
    g345: LineSegment StartX=375.073 StartY=72.4095 StartZ=0 EndX=375.073 EndY=-78.7896 EndZ=0
    g346: ArcOfCircle CenterX=-26.9272 CenterY=22.1087 CenterZ=0 NormalX=0 NormalY=0 NormalZ=1 AngleXU=0 Radius=4 StartAngle=5e-16 EndAngle=3.14159
    g347: LineSegment StartX=-30.9272 StartY=22.1087 StartZ=0 EndX=-34.9272 EndY=-83.7794 EndZ=0
    g348: LineSegment StartX=-18.9272 StartY=-83.7794 StartZ=0 EndX=-22.9272 EndY=22.1087 EndZ=0
  constraints (572):
    c: Coincident(g0,g2)
    c: Block(g0)
    c: Block(g1)
    c: Vertical(g3)
    c: Vertical(g4)
    c: Block(g4)
    c: Block(g3)
    c: Tangent(g6,g7) = 1.5708
    c: Tangent(g7,g9) = 1.5708
    c: Equal(g6,g9)
    c: Coincident(g8,g6)
    c: Coincident(g8,g9)
    c: Block(g7)
    c: Block(g8)
    c: Weight(g10) = 1
    c: Equal(g10,g11)
    c: Equal(g10,g12)
    c: InternalAlignment(g10,g13)
    c: InternalAlignment(g11,g13)
    c: InternalAlignment(g12,g13)
    c: InternalAlignment(g14,g13)
    c: InternalAlignment(g15,g13)
    c: Weight(g16) = 1
    c: Equal(g16,g17)
    c: Equal(g16,g18)
    c: InternalAlignment(g16,g19)
    c: InternalAlignment(g17,g19)
    c: InternalAlignment(g18,g19)
    c: InternalAlignment(g20,g19)
    c: InternalAlignment(g21,g19)
    c: Block(g19)
    c: Block(g13)
    c: Weight(g22) = 1
    c: Equal(g22,g23)
    c: Equal(g22,g24)
    c: InternalAlignment(g22,g25)
    c: InternalAlignment(g23,g25)
    c: InternalAlignment(g24,g25)
    c: InternalAlignment(g26,g25)
    c: InternalAlignment(g27,g25)
    c: Weight(g28) = 1
    c: Equal(g28,g29)
    c: Equal(g28,g30)
    c: InternalAlignment(g28,g31)
    c: InternalAlignment(g29,g31)
    c: InternalAlignment(g30,g31)
    c: InternalAlignment(g32,g31)
    c: InternalAlignment(g33,g31)
    c: Block(g31)
    c: Block(g25)
    c: Weight(g34) = 1
    c: Equal(g34,g35)
    c: Equal(g34,g36)
    c: InternalAlignment(g34,g37)
    c: InternalAlignment(g35,g37)
    c: InternalAlignment(g36,g37)
    c: InternalAlignment(g38,g37)
    c: InternalAlignment(g39,g37)
    c: Weight(g40) = 1
    c: Equal(g40,g41)
    c: Equal(g40,g42)
    c: InternalAlignment(g40,g43)
    c: InternalAlignment(g41,g43)
    c: InternalAlignment(g42,g43)
    c: InternalAlignment(g44,g43)
    c: InternalAlignment(g45,g43)
    c: Block(g37)
    c: Block(g43)
    c: Coincident(g46,g4)
    c: Coincident(g46,g3)
    c: Horizontal(g46)
    c: Distance(g46) = 450
    c: Coincident(g47,g4)
    c: Coincident(g47,g3)
    c: Horizontal(g47)
    c: Horizontal(g48)
    c: Coincident(g2,g48)
    c: Block(g48)
    c: Coincident(g1,g48)
    c: Weight(g49) = 1
    c: Equal(g49,g50)
    c: Equal(g49,g51)
    c: InternalAlignment(g49,g52)
    c: InternalAlignment(g50,g52)
    c: InternalAlignment(g51,g52)
    c: InternalAlignment(g53,g52)
    c: InternalAlignment(g54,g52)
    c: Block(g52)
    c: Weight(g55) = 1
    c: Equal(g55,g56)
    c: Equal(g55,g57)
    c: InternalAlignment(g55,g58)
    c: InternalAlignment(g56,g58)
    c: InternalAlignment(g57,g58)
    c: InternalAlignment(g59,g58)
    c: InternalAlignment(g60,g58)
    c: Block(g58)
    c: Weight(g61) = 1
    c: Equal(g61,g62)
    c: Equal(g61,g63)
    c: InternalAlignment(g61,g64)
    c: InternalAlignment(g62,g64)
    c: InternalAlignment(g63,g64)
    c: InternalAlignment(g65,g64)
    c: InternalAlignment(g66,g64)
    c: Block(g64)
    c: Weight(g67) = 1
    c: Equal(g67,g68)
    c: Equal(g67,g69)
    c: InternalAlignment(g67,g70)
    c: InternalAlignment(g68,g70)
    c: InternalAlignment(g69,g70)
    c: InternalAlignment(g71,g70)
    c: InternalAlignment(g72,g70)
    c: Block(g70)
    c: Weight(g73) = 1
    c: Equal(g73,g74)
    c: Equal(g73,g75)
    c: InternalAlignment(g73,g76)
    c: InternalAlignment(g74,g76)
    c: InternalAlignment(g75,g76)
    c: InternalAlignment(g77,g76)
    c: InternalAlignment(g78,g76)
    c: Weight(g79) = 1
    c: Equal(g79,g80)
    c: Equal(g79,g81)
    c: InternalAlignment(g79,g82)
    c: InternalAlignment(g80,g82)
    c: InternalAlignment(g81,g82)
    c: InternalAlignment(g83,g82)
    c: InternalAlignment(g84,g82)
    c: Block(g76)
    c: Block(g82)
    c: Coincident(g85,g76)
    c: Coincident(g85,g82)
    c: Vertical(g85)
    c: Coincident(g86,g76)
    c: Coincident(g86,g58)
    c: Coincident(g87,g58)
    c: Coincident(g87,g82)
    c: Weight(g88) = 1
    c: Equal(g88,g89)
    c: Equal(g88,g90)
    c: InternalAlignment(g88,g91)
    c: InternalAlignment(g89,g91)
    c: InternalAlignment(g90,g91)
    c: InternalAlignment(g92,g91)
    c: InternalAlignment(g93,g91)
    c: Weight(g94) = 1
    c: Equal(g94,g95)
    c: Equal(g94,g96)
    c: InternalAlignment(g94,g97)
    c: InternalAlignment(g95,g97)
    c: InternalAlignment(g96,g97)
    c: InternalAlignment(g98,g97)
    c: InternalAlignment(g99,g97)
    c: Block(g91)
    c: Block(g97)
    c: Coincident(g100,g91)
    c: Coincident(g100,g97)
    c: Vertical(g100)
    c: Coincident(g101,g91)
    c: Coincident(g101,g52)
    c: Coincident(g102,g52)
    c: Coincident(g102,g97)
    c: Weight(g103) = 1
    c: Equal(g103,g104)
    c: Equal(g103,g105)
    c: InternalAlignment(g103,g106)
    c: InternalAlignment(g104,g106)
    c: InternalAlignment(g105,g106)
    c: InternalAlignment(g107,g106)
    c: InternalAlignment(g108,g106)
    c: Weight(g109) = 1
    c: Equal(g109,g110)
    c: Equal(g109,g111)
    c: InternalAlignment(g109,g112)
    c: InternalAlignment(g110,g112)
    c: InternalAlignment(g111,g112)
    c: InternalAlignment(g113,g112)
    c: InternalAlignment(g114,g112)
    c: Block(g106)
    c: Block(g112)
    c: Coincident(g115,g106)
    c: Coincident(g115,g112)
    c: Vertical(g115)
    c: Coincident(g116,g112)
    c: Coincident(g116,g70)
    c: Coincident(g117,g70)
    c: Coincident(g117,g106)
    c: Weight(g118) = 1
    c: Equal(g118,g119)
    c: Equal(g118,g120)
    c: InternalAlignment(g118,g121)
    c: InternalAlignment(g119,g121)
    c: InternalAlignment(g120,g121)
    c: InternalAlignment(g122,g121)
    c: InternalAlignment(g123,g121)
    c: Weight(g124) = 1
    c: Equal(g124,g125)
    c: Equal(g124,g126)
    c: InternalAlignment(g124,g127)
    c: InternalAlignment(g125,g127)
    c: InternalAlignment(g126,g127)
    c: InternalAlignment(g128,g127)
    c: InternalAlignment(g129,g127)
    c: Block(g121)
    c: Block(g127)
    c: Coincident(g130,g121)
    c: Coincident(g130,g127)
    c: Vertical(g130)
    c: Coincident(g131,g127)
    c: Coincident(g131,g64)
    c: Coincident(g132,g64)
    c: Coincident(g132,g121)
    c: Weight(g133) = 1
    c: Equal(g133,g134)
    c: Equal(g133,g135)
    c: InternalAlignment(g133,g136)
    c: InternalAlignment(g134,g136)
    c: InternalAlignment(g135,g136)
    c: InternalAlignment(g137,g136)
    c: InternalAlignment(g138,g136)
    c: Weight(g139) = 1
    c: Equal(g139,g140)
    c: Equal(g139,g141)
    c: InternalAlignment(g139,g142)
    c: InternalAlignment(g140,g142)
    c: InternalAlignment(g141,g142)
    c: InternalAlignment(g143,g142)
    c: InternalAlignment(g144,g142)
    c: Weight(g145) = 1
    c: Equal(g145,g146)
    c: Equal(g145,g147)
    c: InternalAlignment(g145,g148)
    c: InternalAlignment(g146,g148)
    c: InternalAlignment(g147,g148)
    c: InternalAlignment(g149,g148)
    c: InternalAlignment(g150,g148)
    c: Weight(g151) = 1
    c: Equal(g151,g152)
    c: Equal(g151,g153)
    c: InternalAlignment(g151,g154)
    c: InternalAlignment(g152,g154)
    c: InternalAlignment(g153,g154)
    c: InternalAlignment(g155,g154)
    c: InternalAlignment(g156,g154)
    c: Block(g154)
    c: Block(g148)
    c: Block(g142)
    c: Block(g136)
    c: Coincident(g157,g31)
    c: Coincident(g157,g154)
    c: Coincident(g158,g154)
    c: Coincident(g158,g148)
    c: Horizontal(g158)
    c: Coincident(g159,g148)
    c: Coincident(g159,g31)
    c: Vertical(g159)
    c: Coincident(g160,g25)
    c: Coincident(g160,g142)
    c: Vertical(g160)
    c: Coincident(g161,g142)
    c: Coincident(g161,g136)
    c: Horizontal(g161)
    c: Coincident(g162,g136)
    c: Coincident(g162,g25)
    c: Weight(g163) = 1
    c: Equal(g163,g164)
    c: Equal(g163,g165)
    c: InternalAlignment(g163,g166)
    c: InternalAlignment(g164,g166)
    c: InternalAlignment(g165,g166)
    c: InternalAlignment(g167,g166)
    c: InternalAlignment(g168,g166)
    c: Weight(g169) = 1
    c: Equal(g169,g170)
    c: Equal(g169,g171)
    c: InternalAlignment(g169,g172)
    c: InternalAlignment(g170,g172)
    c: InternalAlignment(g171,g172)
    c: InternalAlignment(g173,g172)
    c: InternalAlignment(g174,g172)
    c: Weight(g175) = 1
    c: Equal(g175,g176)
    c: Equal(g175,g177)
    c: InternalAlignment(g175,g178)
    c: InternalAlignment(g176,g178)
    c: InternalAlignment(g177,g178)
    c: InternalAlignment(g179,g178)
    c: InternalAlignment(g180,g178)
    c: Weight(g181) = 1
    c: Equal(g181,g182)
    c: Equal(g181,g183)
    c: InternalAlignment(g181,g184)
    c: InternalAlignment(g182,g184)
    c: InternalAlignment(g183,g184)
    c: InternalAlignment(g185,g184)
    c: InternalAlignment(g186,g184)
    c: Block(g184)
    c: Block(g178)
    c: Block(g172)
    c: Block(g166)
    c: Coincident(g187,g184)
    c: Coincident(g187,g178)
    c: Horizontal(g187)
    c: Coincident(g188,g178)
    c: Coincident(g188,g13)
    c: Vertical(g188)
    c: Coincident(g189,g19)
    c: Coincident(g189,g172)
    c: Vertical(g189)
    c: Coincident(g190,g172)
    c: Coincident(g190,g166)
    c: Horizontal(g190)
    c: Coincident(g191,g166)
    c: Coincident(g191,g19)
    c: Coincident(g192,g13)
    c: Weight(g193) = 1
    c: Equal(g193,g194)
    c: Equal(g193,g195)
    c: InternalAlignment(g193,g196)
    c: InternalAlignment(g194,g196)
    c: InternalAlignment(g195,g196)
    c: InternalAlignment(g197,g196)
    c: InternalAlignment(g198,g196)
    c: Weight(g199) = 1
    c: Equal(g199,g200)
    c: Equal(g199,g201)
    c: InternalAlignment(g199,g202)
    c: InternalAlignment(g200,g202)
    c: InternalAlignment(g201,g202)
    c: InternalAlignment(g203,g202)
    c: InternalAlignment(g204,g202)
    c: Block(g202)
    c: Block(g196)
    c: Coincident(g205,g202)
    c: Coincident(g205,g37)
    c: Coincident(g206,g37)
    c: Coincident(g206,g196)
    c: Coincident(g207,g196)
    c: Coincident(g207,g202)
    c: Vertical(g207)
    c: Weight(g208) = 1
    c: Equal(g208,g209)
    c: Equal(g208,g210)
    c: InternalAlignment(g208,g211)
    c: InternalAlignment(g209,g211)
    c: InternalAlignment(g210,g211)
    c: InternalAlignment(g212,g211)
    c: InternalAlignment(g213,g211)
    c: Weight(g214) = 1
    c: Equal(g214,g215)
    c: Equal(g214,g216)
    c: InternalAlignment(g214,g217)
    c: InternalAlignment(g215,g217)
    c: InternalAlignment(g216,g217)
    c: InternalAlignment(g218,g217)
    c: InternalAlignment(g219,g217)
    c: Block(g217)
    c: Block(g211)
    c: Coincident(g220,g211)
    c: Coincident(g220,g43)
    c: Coincident(g221,g43)
    c: Coincident(g221,g217)
    c: Coincident(g222,g217)
    c: Coincident(g222,g211)
    c: Vertical(g222)
    c: Horizontal(g223)
    c: Block(g223)
    c: Vertical(g224)
    c: Block(g224)
    c: Block(g225)
    c: Weight(g226) = 1
    c: Equal(g226,g227)
    c: Equal(g226,g228)
    c: InternalAlignment(g226,g229)
    c: InternalAlignment(g227,g229)
    c: InternalAlignment(g228,g229)
    c: InternalAlignment(g230,g229)
    c: InternalAlignment(g231,g229)
    c: Weight(g232) = 1
    c: Equal(g232,g233)
    c: Equal(g232,g234)
    c: InternalAlignment(g232,g235)
    c: InternalAlignment(g233,g235)
    c: InternalAlignment(g234,g235)
    c: InternalAlignment(g236,g235)
    c: InternalAlignment(g237,g235)
    c: Weight(g238) = 1
    c: Equal(g238,g239)
    c: Equal(g238,g240)
    c: InternalAlignment(g238,g241)
    c: InternalAlignment(g239,g241)
    c: InternalAlignment(g240,g241)
    c: InternalAlignment(g242,g241)
    c: InternalAlignment(g243,g241)
    c: Weight(g244) = 1
    c: Equal(g244,g245)
    c: Equal(g244,g246)
    c: InternalAlignment(g244,g247)
    c: InternalAlignment(g245,g247)
    c: InternalAlignment(g246,g247)
    c: InternalAlignment(g248,g247)
    c: InternalAlignment(g249,g247)
    c: Block(g229)
    c: Block(g235)
    c: Block(g241)
    c: Block(g247)
    c: Coincident(g250,g235)
    c: Coincident(g250,g229)
    c: Horizontal(g250)
    c: Block(g192)
    c: Weight(g251) = 1
    c: Equal(g251,g252)
    c: Equal(g251,g253)
    c: InternalAlignment(g251,g254)
    c: InternalAlignment(g252,g254)
    c: InternalAlignment(g253,g254)
    c: InternalAlignment(g255,g254)
    c: InternalAlignment(g256,g254)
    c: Weight(g257) = 1
    c: Equal(g257,g258)
    c: Equal(g257,g259)
    c: InternalAlignment(g257,g260)
    c: InternalAlignment(g258,g260)
    c: InternalAlignment(g259,g260)
    c: InternalAlignment(g261,g260)
    c: InternalAlignment(g262,g260)
    c: Block(g254)
    c: Block(g260)
    c: Coincident(g263,g254)
    c: Coincident(g263,g260)
    c: Weight(g264) = 1
    c: Equal(g264,g265)
    c: Equal(g264,g266)
    c: InternalAlignment(g264,g267)
    c: InternalAlignment(g265,g267)
    c: InternalAlignment(g266,g267)
    c: InternalAlignment(g268,g267)
    c: InternalAlignment(g269,g267)
    c: Weight(g270) = 1
    c: Equal(g270,g271)
    c: Equal(g270,g272)
    c: InternalAlignment(g270,g273)
    c: InternalAlignment(g271,g273)
    c: InternalAlignment(g272,g273)
    c: InternalAlignment(g274,g273)
    c: InternalAlignment(g275,g273)
    c: Weight(g276) = 1
    c: Equal(g276,g277)
    c: Equal(g276,g278)
    c: InternalAlignment(g276,g279)
    c: InternalAlignment(g277,g279)
    c: InternalAlignment(g278,g279)
    c: InternalAlignment(g280,g279)
    c: InternalAlignment(g281,g279)
    c: Block(g279)
    c: Block(g273)
    c: Block(g267)
    c: Coincident(g282,g273)
    c: Coincident(g282,g267)
    c: Coincident(g283,g267)
    c: Coincident(g283,g279)
    c: Vertical(g283)
    c: Coincident(g284,g279)
    c: Coincident(g284,g273)
    c: Horizontal(g284)
    c: Weight(g285) = 1
    c: Equal(g285,g286)
    c: InternalAlignment(g285,g287)
    c: InternalAlignment(g286,g287)
    c: InternalAlignment(g288,g287)
    c: InternalAlignment(g289,g287)
    c: Weight(g290) = 1
    c: InternalAlignment(g291,g293)
    c: InternalAlignment(g292,g293)
    c: InternalAlignment(g294,g293)
    c: InternalAlignment(g295,g293)
    c: Weight(g296) = 1
    c: Equal(g296,g297)
    c: Equal(g296,g298)
    c: InternalAlignment(g296,g299)
    c: InternalAlignment(g297,g299)
    c: InternalAlignment(g298,g299)
    c: InternalAlignment(g300,g299)
    c: InternalAlignment(g301,g299)
    c: Equal(g302,g303)
    c: Equal(g302,g304)
    c: InternalAlignment(g302,g305)
    c: InternalAlignment(g303,g305)
    c: InternalAlignment(g304,g305)
    c: InternalAlignment(g306,g305)
    c: InternalAlignment(g307,g305)
    c: Block(g293)
    c: Block(g299)
    c: Block(g305)
    c: Block(g287)
    c: Coincident(g308,g287)
    c: Coincident(g308,g293)
    c: Horizontal(g308)
    c: Coincident(g309,g293)
    c: Coincident(g309,g299)
    c: Vertical(g309)
    c: Coincident(g310,g299)
    c: Coincident(g310,g305)
    c: Horizontal(g310)
    c: Coincident(g311,g305)
    c: Coincident(g311,g287)
    c: Weight(g312) = 1
    c: Equal(g312,g313)
    c: Equal(g312,g314)
    c: InternalAlignment(g312,g315)
    c: InternalAlignment(g313,g315)
    c: InternalAlignment(g314,g315)
    c: InternalAlignment(g316,g315)
    c: InternalAlignment(g317,g315)
    c: Weight(g318) = 1
    c: Equal(g318,g319)
    c: Equal(g318,g320)
    c: InternalAlignment(g318,g321)
    c: InternalAlignment(g319,g321)
    c: InternalAlignment(g320,g321)
    c: InternalAlignment(g322,g321)
    c: InternalAlignment(g323,g321)
    c: Weight(g324) = 1
    c: Equal(g324,g325)
    c: Equal(g324,g326)
    c: InternalAlignment(g324,g327)
    c: InternalAlignment(g325,g327)
    c: InternalAlignment(g326,g327)
    c: InternalAlignment(g328,g327)
    c: InternalAlignment(g329,g327)
    c: Block(g327)
    c: Block(g321)
    c: Block(g315)
    c: Coincident(g330,g327)
    c: Coincident(g330,g321)
    c: Horizontal(g330)
    c: Coincident(g331,g321)
    c: Coincident(g331,g315)
    c: Vertical(g331)
    c: Coincident(g332,g315)
    c: Coincident(g332,g327)
    c: InternalAlignment(g333,g334)
    c: InternalAlignment(g335,g334)
    c: InternalAlignment(g336,g334)
    c: Block(g334)
    c: Equal(g337,g338)
    c: Equal(g337,g339)
    c: InternalAlignment(g337,g340)
    c: InternalAlignment(g338,g340)
    c: InternalAlignment(g339,g340)
    c: InternalAlignment(g341,g340)
    c: InternalAlignment(g342,g340)
    c: Block(g340)
    c: Coincident(g343,g334)
    c: Horizontal(g343)
    c: Block(g343)
    c: Coincident(g344,g334)
    c: Coincident(g344,g260)
    c: Vertical(g344)
    c: Coincident(g345,g340)
    c: Coincident(g345,g254)
    c: Vertical(g345)
    c: Coincident(g347,g5)
    c: Coincident(g348,g5)
    c: Block(g346)
    c: Block(g5)
    c: Block(g348)
    c: Block(g347)
    c: Distance(g344) = 119.89
FEATURE [Sketcher::SketchObject] Sketch001
  FullyConstrained = true
  MapMode = 4
  Placement = pos=(0,0,0) rot=(0.57735,0.57735,0.57735;2.0944rad)
  Support = -> [Sketch]
  sketch-geometry (46):
    g0: BSplineCurve PolesCount=3 KnotsCount=2 Degree=2 IsPeriodic=0
    g1: ArcOfCircle CenterX=73.1223 CenterY=-32.291 CenterZ=0 NormalX=0 NormalY=0 NormalZ=1 AngleXU=0 Radius=13 StartAngle=5.92268 EndAngle=9.06428
    g2: ArcOfCircle CenterX=66.7816 CenterY=-49.1439 CenterZ=0 NormalX=0 NormalY=0 NormalZ=1 AngleXU=0 Radius=13 StartAngle=2.78068 EndAngle=5.92131
    g3: ArcOfCircle CenterX=55.9263 CenterY=-78.1807 CenterZ=0 NormalX=0 NormalY=0 NormalZ=1 AngleXU=0 Radius=13 StartAngle=5.92268 EndAngle=9.06428
    g4: ArcOfCircle CenterX=49.5884 CenterY=-95.0342 CenterZ=0 NormalX=0 NormalY=0 NormalZ=1 AngleXU=0 Radius=13 StartAngle=2.78068 EndAngle=5.92131
    g5: ArcOfCircle CenterX=38.7206 CenterY=-124.067 CenterZ=0 NormalX=0 NormalY=0 NormalZ=1 AngleXU=0 Radius=13 StartAngle=5.92268 EndAngle=9.06428
    g6: ArcOfCircle CenterX=32.3875 CenterY=-140.92 CenterZ=0 NormalX=0 NormalY=0 NormalZ=1 AngleXU=0 Radius=13 StartAngle=2.78068 EndAngle=5.92131
    g7: ArcOfCircle CenterX=21.4715 CenterY=-169.934 CenterZ=0 NormalX=0 NormalY=0 NormalZ=1 AngleXU=0 Radius=13 StartAngle=5.92268 EndAngle=9.06428
    g8: ArcOfCircle CenterX=15.1336 CenterY=-186.787 CenterZ=0 NormalX=0 NormalY=0 NormalZ=1 AngleXU=0 Radius=13 StartAngle=2.78068 EndAngle=5.92131
    g9-g12: Circle x4 (B-spline internal-alignment scaffolding for g13; pole/knot coordinates omitted)
    g13: BSplineCurve PolesCount=4 KnotsCount=2 Degree=3 IsPeriodic=0
    g14: GeomPoint X=28.8094 Y=-19.0875 Z=0
    g15: GeomPoint X=47.0443 Y=-50.4712 Z=0
    g16: Circle CenterX=53.5586 CenterY=-23.2695 CenterZ=0 NormalX=0 NormalY=0 NormalZ=1 AngleXU=0 Radius=3.24518
    g17: Circle CenterX=-195.441 CenterY=-127.082 CenterZ=0 NormalX=0 NormalY=0 NormalZ=1 AngleXU=0 Radius=1
    g18: Circle CenterX=-8.24091 CenterY=-197.481 CenterZ=0 NormalX=0 NormalY=0 NormalZ=1 AngleXU=0 Radius=1
    g19: Circle CenterX=12.8789 CenterY=-141.321 CenterZ=0 NormalX=0 NormalY=0 NormalZ=1 AngleXU=0 Radius=1
    g20: BSplineCurve PolesCount=3 KnotsCount=2 Degree=2 IsPeriodic=0
    g21: GeomPoint X=-195.441 Y=-127.082 Z=0
    g22: GeomPoint X=12.8789 Y=-141.321 Z=0
    g23: Circle CenterX=-12.8016 CenterY=-179.036 CenterZ=0 NormalX=0 NormalY=0 NormalZ=1 AngleXU=0 Radius=10.5072
    g24: Circle CenterX=0.933922 CenterY=-166.43 CenterZ=0 NormalX=0 NormalY=0 NormalZ=1 AngleXU=0 Radius=3.26661
    g25: Circle CenterX=-33.5518 CenterY=-176.44 CenterZ=0 NormalX=0 NormalY=0 NormalZ=1 AngleXU=0 Radius=5.64388
    g26: Circle CenterX=-47.2366 CenterY=-173.859 CenterZ=0 NormalX=0 NormalY=0 NormalZ=1 AngleXU=0 Radius=3.01653
    g27: Circle CenterX=-56.2595 CenterY=-171.456 CenterZ=0 NormalX=0 NormalY=0 NormalZ=1 AngleXU=0 Radius=2.12826
    g28: ArcOfCircle CenterX=51.2151 CenterY=-198.473 CenterZ=0 NormalX=0 NormalY=0 NormalZ=1 AngleXU=0 Radius=20 StartAngle=2.78189 EndAngle=4.35269
    g29: LineSegment StartX=32.4951 StartY=-191.433 StartZ=0 EndX=94.6578 EndY=-26.1352 EndZ=0
    g30: LineSegment StartX=43.1192 StartY=-220.001 StartZ=0 EndX=-196.497 EndY=-129.89 EndZ=0
    g31: LineSegment StartX=43.1192 StartY=-220.001 StartZ=0 EndX=44.1752 EndY=-217.193 EndZ=0
    g32: LineSegment StartX=117.223 StartY=-19.0875 StartZ=0 EndX=117.223 EndY=-16.0875 EndZ=0
    g33: LineSegment StartX=117.223 StartY=-16.0875 StartZ=0 EndX=17.2232 EndY=-16.0875 EndZ=0
    g34: LineSegment StartX=17.2232 StartY=-16.0875 StartZ=0 EndX=17.2232 EndY=-19.0875 EndZ=0
    g35: LineSegment StartX=28.8094 StartY=-19.0875 StartZ=0 EndX=17.2232 EndY=-19.0875 EndZ=0
    g36: LineSegment StartX=47.0443 StartY=-50.4712 StartZ=0 EndX=12.8789 EndY=-141.321 EndZ=0
    g37: LineSegment StartX=-195.441 StartY=-127.082 StartZ=0 EndX=-196.497 EndY=-129.89 EndZ=0
    g38: LineSegment StartX=85.2866 StartY=-36.8766 StartZ=0 EndX=78.9396 EndY=-53.7463 EndZ=0
    g39: LineSegment StartX=60.9579 StartY=-27.7053 StartZ=0 EndX=54.6191 EndY=-44.5532 EndZ=0
    g40: LineSegment StartX=68.0907 StartY=-82.7664 StartZ=0 EndX=61.7465 EndY=-99.6365 EndZ=0
    g41: LineSegment StartX=43.7619 StartY=-73.595 StartZ=0 EndX=37.426 EndY=-90.4435 EndZ=0
    g42: LineSegment StartX=50.885 StartY=-128.652 StartZ=0 EndX=44.5456 EndY=-145.522 EndZ=0
    g43: LineSegment StartX=26.5562 StartY=-119.481 StartZ=0 EndX=20.2251 EndY=-136.329 EndZ=0
    g44: LineSegment StartX=9.3071 StartY=-165.349 StartZ=0 EndX=2.97115 EndY=-182.197 EndZ=0
    g45: LineSegment StartX=33.6358 StartY=-174.52 StartZ=0 EndX=27.2917 EndY=-191.39 EndZ=0
  constraints (71):
    c: Block(g0)
    c: Block(g1)
    c: Block(g2)
    c: Block(g4)
    c: Block(g3)
    c: Block(g6)
    c: Block(g5)
    c: Block(g8)
    c: Block(g7)
    c: Weight(g9) = 1
    c: Equal(g9,g10)
    c: Equal(g9,g11)
    c: Equal(g9,g12)
    c: InternalAlignment(g9-g12 -> g13) x4
    c: InternalAlignment(g14,g13)
    c: InternalAlignment(g15,g13)
    c: Block(g16)
    c: Weight(g17) = 1
    c: Equal(g17,g18)
    c: Equal(g17,g19)
    c: InternalAlignment(g17,g20)
    c: InternalAlignment(g18,g20)
    c: InternalAlignment(g19,g20)
    c: InternalAlignment(g21,g20)
    c: InternalAlignment(g22,g20)
    c: Block(g20)
    c: Block(g23)
    c: Block(g24)
    c: Block(g25)
    c: Block(g26)
    c: Block(g27)
    c: Block(g28)
    c: Coincident(g29,g28)
    c: Coincident(g29,g0)
    c: Block(g13)
    c: Coincident(g31,g30)
    c: Coincident(g31,g28)
    c: Block(g31)
    c: Coincident(g32,g0)
    c: Vertical(g32)
    c: Coincident(g33,g32)
    c: Horizontal(g33)
    c: Coincident(g34,g33)
    c: Vertical(g34)
    c: Block(g33)
    c: Coincident(g35,g13)
    c: Coincident(g35,g34)
    c: Horizontal(g35)
    c: Coincident(g36,g13)
    c: Coincident(g36,g20)
    c: Coincident(g37,g20)
    c: Coincident(g37,g30)
    c: Block(g30)
    c: Coincident(g38,g1)
    c: Coincident(g38,g2)
    c: Coincident(g39,g1)
    c: Coincident(g39,g2)
    c: Coincident(g40,g3)
    c: Coincident(g40,g4)
    c: Coincident(g41,g3)
    c: Coincident(g41,g4)
    c: Coincident(g42,g5)
    c: Coincident(g42,g6)
    c: Coincident(g43,g5)
    c: Coincident(g43,g6)
    c: Coincident(g44,g7)
    c: Coincident(g44,g8)
    c: Coincident(g45,g7)
    c: Coincident(g45,g8)
    c: Distance(g30) = 256
    c: Distance(g33) = 100
FEATURE [Part::Extrusion] Extrude002
  Base = -> Sketch001
  Dir = (1,0,0)
  DirMode = 2
  FaceMakerClass = Part::FaceMakerBullseye
  LengthFwd = 8
  LengthRev = 0
  Solid = true
  Symmetric = false
FEATURE [Sketcher::SketchObject] Sketch002
  FullyConstrained = true
  sketch-geometry (20):
    g0: LineSegment StartX=-2.77179 StartY=-200.304 StartZ=0 EndX=5.22821 EndY=-200.304 EndZ=0
    g1: LineSegment StartX=5.22821 StartY=-200.304 StartZ=0 EndX=5.22821 EndY=-197.304 EndZ=0
    g2: LineSegment StartX=-2.77179 StartY=-200.304 StartZ=0 EndX=-2.77179 EndY=-197.304 EndZ=0
    g3: LineSegment StartX=5.22821 StartY=-197.304 StartZ=0 EndX=8.22821 EndY=-197.304 EndZ=0
    g4: LineSegment StartX=-2.77179 StartY=-197.304 StartZ=0 EndX=-5.77179 EndY=-197.304 EndZ=0
    g5: LineSegment StartX=19.2282 StartY=-203.304 StartZ=0 EndX=19.2282 EndY=-206.304 EndZ=0
    g6: LineSegment StartX=-16.7718 StartY=-203.304 StartZ=0 EndX=-16.7718 EndY=-206.304 EndZ=0
    g7: LineSegment StartX=-16.7718 StartY=-206.304 StartZ=0 EndX=19.2282 EndY=-206.304 EndZ=0
    g8: Circle CenterX=-16.7718 CenterY=-203.304 CenterZ=0 NormalX=0 NormalY=0 NormalZ=1 AngleXU=0 Radius=1
    g9: Circle CenterX=-5.77179 CenterY=-203.304 CenterZ=0 NormalX=0 NormalY=0 NormalZ=1 AngleXU=0 Radius=1
    g10: Circle CenterX=-5.77179 CenterY=-197.304 CenterZ=0 NormalX=0 NormalY=0 NormalZ=1 AngleXU=0 Radius=1
    g11: BSplineCurve PolesCount=3 KnotsCount=2 Degree=2 IsPeriodic=0
    g12: GeomPoint X=-16.7718 Y=-203.304 Z=0
    g13: GeomPoint X=-5.77179 Y=-197.304 Z=0
    g14: Circle CenterX=19.2282 CenterY=-203.304 CenterZ=0 NormalX=0 NormalY=0 NormalZ=1 AngleXU=0 Radius=1
    g15: Circle CenterX=8.22821 CenterY=-203.304 CenterZ=0 NormalX=0 NormalY=0 NormalZ=1 AngleXU=0 Radius=1
    g16: Circle CenterX=8.22821 CenterY=-197.304 CenterZ=0 NormalX=0 NormalY=0 NormalZ=1 AngleXU=0 Radius=1
    g17: BSplineCurve PolesCount=3 KnotsCount=2 Degree=2 IsPeriodic=0
    g18: GeomPoint X=19.2282 Y=-203.304 Z=0
    g19: GeomPoint X=8.22821 Y=-197.304 Z=0
  constraints (41):
    c: Horizontal(g0)
    c: Distance(g0) = 8
    c: Coincident(g1,g0)
    c: Vertical(g1)
    c: Distance(g1) = 3
    c: Coincident(g2,g0)
    c: Vertical(g2)
    c: Distance(g2) = 3
    c: Coincident(g3,g1)
    c: Horizontal(g3)
    c: Distance(g3) = 3
    c: Coincident(g4,g2)
    c: Horizontal(g4)
    c: Distance(g4) = 3
    c: Vertical(g5)
    c: Vertical(g6)
    c: Coincident(g7,g6)
    c: Coincident(g7,g5)
    c: Weight(g8) = 1
    c: Equal(g8,g9)
    c: Equal(g8,g10)
    c: Coincident(g11,g4)
    c: InternalAlignment(g8,g11)
    c: InternalAlignment(g9,g11)
    c: InternalAlignment(g10,g11)
    c: InternalAlignment(g12,g11)
    c: InternalAlignment(g13,g11)
    c: Coincident(g17,g5)
    c: Weight(g14) = 1
    c: Equal(g14,g15)
    c: Equal(g14,g16)
    c: Coincident(g17,g3)
    c: InternalAlignment(g14,g17)
    c: InternalAlignment(g15,g17)
    c: InternalAlignment(g16,g17)
    c: InternalAlignment(g18,g17)
    c: InternalAlignment(g19,g17)
    c: Block(g7)
    c: Block(g17)
    c: Block(g11)
    c: Block(g6)
FEATURE [Part::Extrusion] Extrude003
  Base = -> Sketch002
  Dir = (0,0,1)
  DirMode = 2
  FaceMakerClass = Part::FaceMakerBullseye
  LengthFwd = 260
  LengthRev = 0
  Solid = true
  Symmetric = false
FEATURE [Part::Extrusion] Extrude
  Base = -> Sketch
  Dir = (0,0,1)
  DirMode = 2
  FaceMakerClass = Part::FaceMakerBullseye
  LengthFwd = 14
  LengthRev = 0
  Solid = true
  Symmetric = false
FEATURE [Sketcher::SketchObject] Sketch003
  FullyConstrained = false
  sketch-geometry (357):
    g0: LineSegment StartX=-10.9272 StartY=-82.7794 StartZ=0 EndX=46.0728 EndY=-51.4823 EndZ=0
    g1: LineSegment StartX=-10.9272 StartY=76.4095 StartZ=0 EndX=-10.9272 EndY=-82.7794 EndZ=0
    g2: LineSegment StartX=46.0728 StartY=76.4095 StartZ=0 EndX=46.0728 EndY=-51.4823 EndZ=0
    g3: LineSegment StartX=-42.9272 StartY=136.221 StartZ=0 EndX=-42.9272 EndY=-103.779 EndZ=0
    g4: LineSegment StartX=407.073 StartY=136.221 StartZ=0 EndX=407.073 EndY=-103.779 EndZ=0
    g5: ArcOfCircle CenterX=-26.9272 CenterY=-83.7794 CenterZ=0 NormalX=0 NormalY=0 NormalZ=1 AngleXU=0 Radius=8 StartAngle=3.14159 EndAngle=6.28319
    g6: ArcOfCircle CenterX=391.073 CenterY=-83.7794 CenterZ=0 NormalX=0 NormalY=0 NormalZ=1 AngleXU=0 Radius=8 StartAngle=3.14159 EndAngle=6.28319
    g7: Circle CenterX=175.022 CenterY=27.0628 CenterZ=0 NormalX=0 NormalY=0 NormalZ=1 AngleXU=0 Radius=1
    g8: Circle CenterX=179.022 CenterY=24.8665 CenterZ=0 NormalX=0 NormalY=0 NormalZ=1 AngleXU=0 Radius=1
    g9: Circle CenterX=179.022 CenterY=27.0628 CenterZ=0 NormalX=0 NormalY=0 NormalZ=1 AngleXU=0 Radius=1
    g10: BSplineCurve PolesCount=3 KnotsCount=2 Degree=2 IsPeriodic=0
    g11: GeomPoint X=175.022 Y=27.0628 Z=0
    g12: GeomPoint X=179.022 Y=27.0628 Z=0
    g13: Circle CenterX=189.124 CenterY=27.0628 CenterZ=0 NormalX=0 NormalY=0 NormalZ=1 AngleXU=0 Radius=1
    g14: Circle CenterX=185.124 CenterY=24.8665 CenterZ=0 NormalX=0 NormalY=0 NormalZ=1 AngleXU=0 Radius=1
    g15: Circle CenterX=185.124 CenterY=27.0628 CenterZ=0 NormalX=0 NormalY=0 NormalZ=1 AngleXU=0 Radius=1
    g16: BSplineCurve PolesCount=3 KnotsCount=2 Degree=2 IsPeriodic=0
    g17: GeomPoint X=189.124 Y=27.0628 Z=0
    g18: GeomPoint X=185.124 Y=27.0628 Z=0
    g19: Circle CenterX=175.022 CenterY=5.37834 CenterZ=0 NormalX=0 NormalY=0 NormalZ=1 AngleXU=0 Radius=1
    g20: Circle CenterX=179.022 CenterY=7.57463 CenterZ=0 NormalX=0 NormalY=0 NormalZ=1 AngleXU=0 Radius=1
    g21: Circle CenterX=179.022 CenterY=5.34704 CenterZ=0 NormalX=0 NormalY=0 NormalZ=1 AngleXU=0 Radius=1
    g22: BSplineCurve PolesCount=3 KnotsCount=2 Degree=2 IsPeriodic=0
    g23: GeomPoint X=175.022 Y=5.37834 Z=0
    g24: GeomPoint X=179.022 Y=5.34704 Z=0
    g25: Circle CenterX=189.124 CenterY=5.37834 CenterZ=0 NormalX=0 NormalY=0 NormalZ=1 AngleXU=0 Radius=1
    g26: Circle CenterX=185.124 CenterY=7.57463 CenterZ=0 NormalX=0 NormalY=0 NormalZ=1 AngleXU=0 Radius=1
    g27: Circle CenterX=185.124 CenterY=5.34704 CenterZ=0 NormalX=0 NormalY=0 NormalZ=1 AngleXU=0 Radius=1
    g28: BSplineCurve PolesCount=3 KnotsCount=2 Degree=2 IsPeriodic=0
    g29: GeomPoint X=189.124 Y=5.37834 Z=0
    g30: GeomPoint X=185.124 Y=5.34704 Z=0
    g31: Circle CenterX=165.871 CenterY=18.1458 CenterZ=0 NormalX=0 NormalY=0 NormalZ=1 AngleXU=0 Radius=1
    g32: Circle CenterX=169.377 CenterY=16.2206 CenterZ=0 NormalX=0 NormalY=0 NormalZ=1 AngleXU=0 Radius=1
    g33: Circle CenterX=165.871 CenterY=14.2954 CenterZ=0 NormalX=0 NormalY=0 NormalZ=1 AngleXU=0 Radius=1
    g34: BSplineCurve PolesCount=3 KnotsCount=2 Degree=2 IsPeriodic=0
    g35: GeomPoint X=165.871 Y=18.1458 Z=0
    g36: GeomPoint X=165.871 Y=14.2954 Z=0
    g37: Circle CenterX=198.275 CenterY=18.1458 CenterZ=0 NormalX=0 NormalY=0 NormalZ=1 AngleXU=0 Radius=1
    g38: Circle CenterX=194.768 CenterY=16.2206 CenterZ=0 NormalX=0 NormalY=0 NormalZ=1 AngleXU=0 Radius=1
    g39: Circle CenterX=198.275 CenterY=14.2954 CenterZ=0 NormalX=0 NormalY=0 NormalZ=1 AngleXU=0 Radius=1
    g40: BSplineCurve PolesCount=3 KnotsCount=2 Degree=2 IsPeriodic=0
    g41: GeomPoint X=198.275 Y=18.1458 Z=0
    g42: GeomPoint X=198.275 Y=14.2954 Z=0
    g43: LineSegment StartX=407.073 StartY=-103.779 StartZ=0 EndX=-42.9272 EndY=-103.779 EndZ=0
    g44: LineSegment StartX=407.073 StartY=136.221 StartZ=0 EndX=-42.9272 EndY=136.221 EndZ=0
    g45: LineSegment StartX=46.0728 StartY=76.4095 StartZ=0 EndX=-10.9272 EndY=76.4095 EndZ=0
    g46: Circle CenterX=125.607 CenterY=54.1951 CenterZ=0 NormalX=0 NormalY=0 NormalZ=1 AngleXU=0 Radius=1
    g47: Circle CenterX=139.632 CenterY=46.4944 CenterZ=0 NormalX=0 NormalY=0 NormalZ=1 AngleXU=0 Radius=1
    g48: Circle CenterX=127.326 CenterY=56.7187 CenterZ=0 NormalX=0 NormalY=0 NormalZ=1 AngleXU=0 Radius=1
    g49: BSplineCurve PolesCount=3 KnotsCount=2 Degree=2 IsPeriodic=0
    g50: GeomPoint X=125.607 Y=54.1951 Z=0
    g51: GeomPoint X=127.326 Y=56.7187 Z=0
    g52: Circle CenterX=236.821 CenterY=56.7187 CenterZ=0 NormalX=0 NormalY=0 NormalZ=1 AngleXU=0 Radius=1
    g53: Circle CenterX=224.513 CenterY=46.4944 CenterZ=0 NormalX=0 NormalY=0 NormalZ=1 AngleXU=0 Radius=1
    g54: Circle CenterX=238.538 CenterY=54.1951 CenterZ=0 NormalX=0 NormalY=0 NormalZ=1 AngleXU=0 Radius=1
    g55: BSplineCurve PolesCount=3 KnotsCount=2 Degree=2 IsPeriodic=0
    g56: GeomPoint X=236.821 Y=56.7187 Z=0
    g57: GeomPoint X=238.538 Y=54.1951 Z=0
    g58: Circle CenterX=238.538 CenterY=-21.7539 CenterZ=0 NormalX=0 NormalY=0 NormalZ=1 AngleXU=0 Radius=1
    g59: Circle CenterX=224.513 CenterY=-14.0532 CenterZ=0 NormalX=0 NormalY=0 NormalZ=1 AngleXU=0 Radius=1
    g60: Circle CenterX=236.821 CenterY=-24.2775 CenterZ=0 NormalX=0 NormalY=0 NormalZ=1 AngleXU=0 Radius=1
    g61: BSplineCurve PolesCount=3 KnotsCount=2 Degree=2 IsPeriodic=0
    g62: GeomPoint X=238.538 Y=-21.7539 Z=0
    g63: GeomPoint X=236.821 Y=-24.2775 Z=0
    g64: Circle CenterX=125.607 CenterY=-21.7539 CenterZ=0 NormalX=0 NormalY=0 NormalZ=1 AngleXU=0 Radius=1
    g65: Circle CenterX=139.632 CenterY=-14.0532 CenterZ=0 NormalX=0 NormalY=0 NormalZ=1 AngleXU=0 Radius=1
    g66: Circle CenterX=127.325 CenterY=-24.2775 CenterZ=0 NormalX=0 NormalY=0 NormalZ=1 AngleXU=0 Radius=1
    g67: BSplineCurve PolesCount=3 KnotsCount=2 Degree=2 IsPeriodic=0
    g68: GeomPoint X=125.607 Y=-21.7539 Z=0
    g69: GeomPoint X=127.325 Y=-24.2775 Z=0
    g70: Circle CenterX=302.996 CenterY=111.695 CenterZ=0 NormalX=0 NormalY=0 NormalZ=1 AngleXU=0 Radius=1
    g71: Circle CenterX=306.073 CenterY=114.251 CenterZ=0 NormalX=0 NormalY=0 NormalZ=1 AngleXU=0 Radius=1
    g72: Circle CenterX=306.073 CenterY=110.251 CenterZ=0 NormalX=0 NormalY=0 NormalZ=1 AngleXU=0 Radius=1
    g73: BSplineCurve PolesCount=3 KnotsCount=2 Degree=2 IsPeriodic=0
    g74: GeomPoint X=302.996 Y=111.695 Z=0
    g75: GeomPoint X=306.073 Y=110.251 Z=0
    g76: Circle CenterX=306.073 CenterY=95.2763 CenterZ=0 NormalX=0 NormalY=0 NormalZ=1 AngleXU=0 Radius=1
    g77: Circle CenterX=306.073 CenterY=91.2763 CenterZ=0 NormalX=0 NormalY=0 NormalZ=1 AngleXU=0 Radius=1
    g78: Circle CenterX=302.567 CenterY=89.3511 CenterZ=0 NormalX=0 NormalY=0 NormalZ=1 AngleXU=0 Radius=1
    g79: BSplineCurve PolesCount=3 KnotsCount=2 Degree=2 IsPeriodic=0
    g80: GeomPoint X=306.073 Y=95.2763 Z=0
    g81: GeomPoint X=302.567 Y=89.3511 Z=0
    g82: LineSegment StartX=306.073 StartY=110.251 StartZ=0 EndX=306.073 EndY=95.2763 EndZ=0
    g83: LineSegment StartX=302.996 StartY=111.695 StartZ=0 EndX=236.821 EndY=56.7187 EndZ=0
    g84: LineSegment StartX=238.538 StartY=54.1951 StartZ=0 EndX=302.567 EndY=89.3511 EndZ=0
    g85: Circle CenterX=61.1496 CenterY=111.695 CenterZ=0 NormalX=0 NormalY=0 NormalZ=1 AngleXU=0 Radius=1
    g86: Circle CenterX=58.0728 CenterY=114.251 CenterZ=0 NormalX=0 NormalY=0 NormalZ=1 AngleXU=0 Radius=1
    g87: Circle CenterX=58.0728 CenterY=110.251 CenterZ=0 NormalX=0 NormalY=0 NormalZ=1 AngleXU=0 Radius=1
    g88: BSplineCurve PolesCount=3 KnotsCount=2 Degree=2 IsPeriodic=0
    g89: GeomPoint X=61.1496 Y=111.695 Z=0
    g90: GeomPoint X=58.0728 Y=110.251 Z=0
    g91: Circle CenterX=61.5791 CenterY=89.3511 CenterZ=0 NormalX=0 NormalY=0 NormalZ=1 AngleXU=0 Radius=1
    g92: Circle CenterX=58.0728 CenterY=91.2763 CenterZ=0 NormalX=0 NormalY=0 NormalZ=1 AngleXU=0 Radius=1
    g93: Circle CenterX=58.0728 CenterY=95.2763 CenterZ=0 NormalX=0 NormalY=0 NormalZ=1 AngleXU=0 Radius=1
    g94: BSplineCurve PolesCount=3 KnotsCount=2 Degree=2 IsPeriodic=0
    g95: GeomPoint X=61.5791 Y=89.3511 Z=0
    g96: GeomPoint X=58.0728 Y=95.2763 Z=0
    g97: LineSegment StartX=58.0728 StartY=110.251 StartZ=0 EndX=58.0728 EndY=95.2763 EndZ=0
    g98: LineSegment StartX=61.1496 StartY=111.695 StartZ=0 EndX=127.326 EndY=56.7187 EndZ=0
    g99: LineSegment StartX=125.607 StartY=54.1951 StartZ=0 EndX=61.5791 EndY=89.3511 EndZ=0
    g100: Circle CenterX=61.5791 CenterY=-56.9099 CenterZ=0 NormalX=0 NormalY=0 NormalZ=1 AngleXU=0 Radius=1
    g101: Circle CenterX=58.0728 CenterY=-58.8351 CenterZ=0 NormalX=0 NormalY=0 NormalZ=1 AngleXU=0 Radius=1
    g102: Circle CenterX=58.0728 CenterY=-62.8351 CenterZ=0 NormalX=0 NormalY=0 NormalZ=1 AngleXU=0 Radius=1
    g103: BSplineCurve PolesCount=3 KnotsCount=2 Degree=2 IsPeriodic=0
    g104: GeomPoint X=61.5791 Y=-56.9099 Z=0
    g105: GeomPoint X=58.0728 Y=-62.8351 Z=0
    g106: Circle CenterX=58.0728 CenterY=-77.8102 CenterZ=0 NormalX=0 NormalY=0 NormalZ=1 AngleXU=0 Radius=1
    g107: Circle CenterX=58.0728 CenterY=-81.8102 CenterZ=0 NormalX=0 NormalY=0 NormalZ=1 AngleXU=0 Radius=1
    g108: Circle CenterX=61.1496 CenterY=-79.2541 CenterZ=0 NormalX=0 NormalY=0 NormalZ=1 AngleXU=0 Radius=1
    g109: BSplineCurve PolesCount=3 KnotsCount=2 Degree=2 IsPeriodic=0
    g110: GeomPoint X=58.0728 Y=-77.8102 Z=0
    g111: GeomPoint X=61.1496 Y=-79.2541 Z=0
    g112: LineSegment StartX=58.0728 StartY=-62.8351 StartZ=0 EndX=58.0728 EndY=-77.8102 EndZ=0
    g113: LineSegment StartX=61.1496 StartY=-79.2541 StartZ=0 EndX=127.325 EndY=-24.2775 EndZ=0
    g114: LineSegment StartX=125.607 StartY=-21.7539 StartZ=0 EndX=61.5791 EndY=-56.9099 EndZ=0
    g115: Circle CenterX=302.567 CenterY=-56.9099 CenterZ=0 NormalX=0 NormalY=0 NormalZ=1 AngleXU=0 Radius=1
    g116: Circle CenterX=306.073 CenterY=-58.8351 CenterZ=0 NormalX=0 NormalY=0 NormalZ=1 AngleXU=0 Radius=1
    g117: Circle CenterX=306.073 CenterY=-62.8351 CenterZ=0 NormalX=0 NormalY=0 NormalZ=1 AngleXU=0 Radius=1
    g118: BSplineCurve PolesCount=3 KnotsCount=2 Degree=2 IsPeriodic=0
    g119: GeomPoint X=302.567 Y=-56.9099 Z=0
    g120: GeomPoint X=306.073 Y=-62.8351 Z=0
    g121: Circle CenterX=302.996 CenterY=-79.2541 CenterZ=0 NormalX=0 NormalY=0 NormalZ=1 AngleXU=0 Radius=1
    g122: Circle CenterX=306.073 CenterY=-81.8102 CenterZ=0 NormalX=0 NormalY=0 NormalZ=1 AngleXU=0 Radius=1
    g123: Circle CenterX=306.073 CenterY=-77.8102 CenterZ=0 NormalX=0 NormalY=0 NormalZ=1 AngleXU=0 Radius=1
    g124: BSplineCurve PolesCount=3 KnotsCount=2 Degree=2 IsPeriodic=0
    g125: GeomPoint X=302.996 Y=-79.2541 Z=0
    g126: GeomPoint X=306.073 Y=-77.8102 Z=0
    g127: LineSegment StartX=306.073 StartY=-62.8351 StartZ=0 EndX=306.073 EndY=-77.8102 EndZ=0
    g128: LineSegment StartX=302.996 StartY=-79.2541 StartZ=0 EndX=236.821 EndY=-24.2775 EndZ=0
    g129: LineSegment StartX=238.538 StartY=-21.7539 StartZ=0 EndX=302.567 EndY=-56.9099 EndZ=0
    g130: Circle CenterX=61.6457 CenterY=-88.8112 CenterZ=0 NormalX=0 NormalY=0 NormalZ=1 AngleXU=0 Radius=1
    g131: Circle CenterX=58.0728 CenterY=-91.7794 CenterZ=0 NormalX=0 NormalY=0 NormalZ=1 AngleXU=0 Radius=1
    g132: Circle CenterX=63.9135 CenterY=-91.7794 CenterZ=0 NormalX=0 NormalY=0 NormalZ=1 AngleXU=0 Radius=1
    g133: BSplineCurve PolesCount=3 KnotsCount=2 Degree=2 IsPeriodic=0
    g134: GeomPoint X=61.6457 Y=-88.8112 Z=0
    g135: GeomPoint X=63.9135 Y=-91.7794 Z=0
    g136: Circle CenterX=179.022 CenterY=-85.8163 CenterZ=0 NormalX=0 NormalY=0 NormalZ=1 AngleXU=0 Radius=1
    g137: Circle CenterX=179.022 CenterY=-91.7794 CenterZ=0 NormalX=0 NormalY=0 NormalZ=1 AngleXU=0 Radius=1
    g138: Circle CenterX=171.895 CenterY=-91.7794 CenterZ=0 NormalX=0 NormalY=0 NormalZ=1 AngleXU=0 Radius=1
    g139: BSplineCurve PolesCount=3 KnotsCount=2 Degree=2 IsPeriodic=0
    g140: GeomPoint X=179.022 Y=-85.8163 Z=0
    g141: GeomPoint X=171.895 Y=-91.7794 Z=0
    g142: Circle CenterX=185.124 CenterY=-86.2028 CenterZ=0 NormalX=0 NormalY=0 NormalZ=1 AngleXU=0 Radius=1
    g143: Circle CenterX=185.124 CenterY=-91.7794 CenterZ=0 NormalX=0 NormalY=0 NormalZ=1 AngleXU=0 Radius=1
    g144: Circle CenterX=191.747 CenterY=-91.7794 CenterZ=0 NormalX=0 NormalY=0 NormalZ=1 AngleXU=0 Radius=1
    g145: BSplineCurve PolesCount=3 KnotsCount=2 Degree=2 IsPeriodic=0
    g146: GeomPoint X=185.124 Y=-86.2028 Z=0
    g147: GeomPoint X=191.747 Y=-91.7794 Z=0
    g148: Circle CenterX=299.888 CenterY=-86.6413 CenterZ=0 NormalX=0 NormalY=0 NormalZ=1 AngleXU=0 Radius=1
    g149: Circle CenterX=306.073 CenterY=-91.7794 CenterZ=0 NormalX=0 NormalY=0 NormalZ=1 AngleXU=0 Radius=1
    g150: Circle CenterX=298.776 CenterY=-91.7794 CenterZ=0 NormalX=0 NormalY=0 NormalZ=1 AngleXU=0 Radius=1
    g151: BSplineCurve PolesCount=3 KnotsCount=2 Degree=2 IsPeriodic=0
    g152: GeomPoint X=299.888 Y=-86.6413 Z=0
    g153: GeomPoint X=298.776 Y=-91.7794 Z=0
    g154: LineSegment StartX=189.124 StartY=5.37834 StartZ=0 EndX=299.888 EndY=-86.6413 EndZ=0
    g155: LineSegment StartX=298.776 StartY=-91.7794 StartZ=0 EndX=191.747 EndY=-91.7794 EndZ=0
    g156: LineSegment StartX=185.124 StartY=-86.2028 StartZ=0 EndX=185.124 EndY=5.34704 EndZ=0
    g157: LineSegment StartX=179.022 StartY=5.34704 StartZ=0 EndX=179.022 EndY=-85.8163 EndZ=0
    g158: LineSegment StartX=171.895 StartY=-91.7794 StartZ=0 EndX=63.9135 EndY=-91.7794 EndZ=0
    g159: LineSegment StartX=61.6457 StartY=-88.8112 StartZ=0 EndX=175.022 EndY=5.37834 EndZ=0
    g160: Circle CenterX=302.073 CenterY=124.221 CenterZ=0 NormalX=0 NormalY=0 NormalZ=1 AngleXU=0 Radius=1
    g161: Circle CenterX=306.073 CenterY=124.221 CenterZ=0 NormalX=0 NormalY=0 NormalZ=1 AngleXU=0 Radius=1
    g162: Circle CenterX=302.996 CenterY=121.665 CenterZ=0 NormalX=0 NormalY=0 NormalZ=1 AngleXU=0 Radius=1
    g163: BSplineCurve PolesCount=3 KnotsCount=2 Degree=2 IsPeriodic=0
    g164: GeomPoint X=302.073 Y=124.221 Z=0
    g165: GeomPoint X=302.996 Y=121.665 Z=0
    g166: Circle CenterX=189.124 CenterY=124.221 CenterZ=0 NormalX=0 NormalY=0 NormalZ=1 AngleXU=0 Radius=1
    g167: Circle CenterX=185.124 CenterY=124.221 CenterZ=0 NormalX=0 NormalY=0 NormalZ=1 AngleXU=0 Radius=1
    g168: Circle CenterX=185.124 CenterY=120.221 CenterZ=0 NormalX=0 NormalY=0 NormalZ=1 AngleXU=0 Radius=1
    g169: BSplineCurve PolesCount=3 KnotsCount=2 Degree=2 IsPeriodic=0
    g170: GeomPoint X=189.124 Y=124.221 Z=0
    g171: GeomPoint X=185.124 Y=120.221 Z=0
    g172: Circle CenterX=175.022 CenterY=124.221 CenterZ=0 NormalX=0 NormalY=0 NormalZ=1 AngleXU=0 Radius=1
    g173: Circle CenterX=179.022 CenterY=124.221 CenterZ=0 NormalX=0 NormalY=0 NormalZ=1 AngleXU=0 Radius=1
    g174: Circle CenterX=179.022 CenterY=120.221 CenterZ=0 NormalX=0 NormalY=0 NormalZ=1 AngleXU=0 Radius=1
    g175: BSplineCurve PolesCount=3 KnotsCount=2 Degree=2 IsPeriodic=0
    g176: GeomPoint X=175.022 Y=124.221 Z=0
    g177: GeomPoint X=179.022 Y=120.221 Z=0
    g178: Circle CenterX=62.0728 CenterY=124.221 CenterZ=0 NormalX=0 NormalY=0 NormalZ=1 AngleXU=0 Radius=1
    g179: Circle CenterX=58.0728 CenterY=124.221 CenterZ=0 NormalX=0 NormalY=0 NormalZ=1 AngleXU=0 Radius=1
    g180: Circle CenterX=61.1496 CenterY=121.665 CenterZ=0 NormalX=0 NormalY=0 NormalZ=1 AngleXU=0 Radius=1
    g181: BSplineCurve PolesCount=3 KnotsCount=2 Degree=2 IsPeriodic=0
    g182: GeomPoint X=62.0728 Y=124.221 Z=0
    g183: GeomPoint X=61.1496 Y=121.665 Z=0
    g184: LineSegment StartX=62.0728 StartY=124.221 StartZ=0 EndX=175.022 EndY=124.221 EndZ=0
    g185: LineSegment StartX=179.022 StartY=120.221 StartZ=0 EndX=179.022 EndY=27.0628 EndZ=0
    g186: LineSegment StartX=185.124 StartY=27.0628 StartZ=0 EndX=185.124 EndY=120.221 EndZ=0
    g187: LineSegment StartX=189.124 StartY=124.221 StartZ=0 EndX=302.073 EndY=124.221 EndZ=0
    g188: LineSegment StartX=302.996 StartY=121.665 StartZ=0 EndX=189.124 EndY=27.0628 EndZ=0
    g189: LineSegment StartX=175.022 StartY=27.0628 StartZ=0 EndX=61.1496 EndY=121.665 EndZ=0
    g190: Circle CenterX=61.5791 CenterY=75.4095 CenterZ=0 NormalX=0 NormalY=0 NormalZ=1 AngleXU=0 Radius=1
    g191: Circle CenterX=58.0728 CenterY=77.3346 CenterZ=0 NormalX=0 NormalY=0 NormalZ=1 AngleXU=0 Radius=1
    g192: Circle CenterX=58.0728 CenterY=73.3346 CenterZ=0 NormalX=0 NormalY=0 NormalZ=1 AngleXU=0 Radius=1
    g193: BSplineCurve PolesCount=3 KnotsCount=2 Degree=2 IsPeriodic=0
    g194: GeomPoint X=61.5791 Y=75.4095 Z=0
    g195: GeomPoint X=58.0728 Y=73.3346 Z=0
    g196: Circle CenterX=58.0728 CenterY=-40.8935 CenterZ=0 NormalX=0 NormalY=0 NormalZ=1 AngleXU=0 Radius=1
    g197: Circle CenterX=58.0728 CenterY=-44.8935 CenterZ=0 NormalX=0 NormalY=0 NormalZ=1 AngleXU=0 Radius=1
    g198: Circle CenterX=61.5791 CenterY=-42.9683 CenterZ=0 NormalX=0 NormalY=0 NormalZ=1 AngleXU=0 Radius=1
    g199: BSplineCurve PolesCount=3 KnotsCount=2 Degree=2 IsPeriodic=0
    g200: GeomPoint X=58.0728 Y=-40.8935 Z=0
    g201: GeomPoint X=61.5791 Y=-42.9683 Z=0
    g202: LineSegment StartX=61.5791 StartY=-42.9683 StartZ=0 EndX=165.871 EndY=14.2954 EndZ=0
    g203: LineSegment StartX=165.871 StartY=18.1458 StartZ=0 EndX=61.5791 EndY=75.4095 EndZ=0
    g204: LineSegment StartX=58.0728 StartY=73.3346 StartZ=0 EndX=58.0728 EndY=-40.8935 EndZ=0
    g205: Circle CenterX=302.567 CenterY=-42.9683 CenterZ=0 NormalX=0 NormalY=0 NormalZ=1 AngleXU=0 Radius=1
    g206: Circle CenterX=306.073 CenterY=-44.8935 CenterZ=0 NormalX=0 NormalY=0 NormalZ=1 AngleXU=0 Radius=1
    g207: Circle CenterX=306.073 CenterY=-40.8935 CenterZ=0 NormalX=0 NormalY=0 NormalZ=1 AngleXU=0 Radius=1
    g208: BSplineCurve PolesCount=3 KnotsCount=2 Degree=2 IsPeriodic=0
    g209: GeomPoint X=302.567 Y=-42.9683 Z=0
    g210: GeomPoint X=306.073 Y=-40.8935 Z=0
    g211: Circle CenterX=306.073 CenterY=73.3346 CenterZ=0 NormalX=0 NormalY=0 NormalZ=1 AngleXU=0 Radius=1
    g212: Circle CenterX=306.073 CenterY=77.3346 CenterZ=0 NormalX=0 NormalY=0 NormalZ=1 AngleXU=0 Radius=1
    g213: Circle CenterX=302.567 CenterY=75.4095 CenterZ=0 NormalX=0 NormalY=0 NormalZ=1 AngleXU=0 Radius=1
    g214: BSplineCurve PolesCount=3 KnotsCount=2 Degree=2 IsPeriodic=0
    g215: GeomPoint X=306.073 Y=73.3346 Z=0
    g216: GeomPoint X=302.567 Y=75.4095 Z=0
    g217: LineSegment StartX=302.567 StartY=-42.9683 StartZ=0 EndX=198.275 EndY=14.2954 EndZ=0
    g218: LineSegment StartX=198.275 StartY=18.1458 StartZ=0 EndX=302.567 EndY=75.4095 EndZ=0
    g219: LineSegment StartX=306.073 StartY=73.3346 StartZ=0 EndX=306.073 EndY=-40.8935 EndZ=0
    g220: LineSegment StartX=322.073 StartY=105.865 StartZ=0 EndX=328.643 EndY=105.865 EndZ=0
    g221: LineSegment StartX=318.073 StartY=120.221 StartZ=0 EndX=318.073 EndY=109.865 EndZ=0
    g222: LineSegment StartX=336.157 StartY=107.779 StartZ=0 EndX=362.567 EndY=122.294 EndZ=0
    g223: Circle CenterX=362.073 CenterY=124.221 CenterZ=0 NormalX=0 NormalY=0 NormalZ=1 AngleXU=0 Radius=1
    g224: Circle CenterX=366.073 CenterY=124.221 CenterZ=0 NormalX=0 NormalY=0 NormalZ=1 AngleXU=0 Radius=1
    g225: Circle CenterX=362.567 CenterY=122.294 CenterZ=0 NormalX=0 NormalY=0 NormalZ=1 AngleXU=0 Radius=1
    g226: BSplineCurve PolesCount=3 KnotsCount=2 Degree=2 IsPeriodic=0
    g227: GeomPoint X=362.073 Y=124.221 Z=0
    g228: GeomPoint X=362.567 Y=122.294 Z=0
    g229: Circle CenterX=322.073 CenterY=124.221 CenterZ=0 NormalX=0 NormalY=0 NormalZ=1 AngleXU=0 Radius=1
    g230: Circle CenterX=318.073 CenterY=124.221 CenterZ=0 NormalX=0 NormalY=0 NormalZ=1 AngleXU=0 Radius=1
    g231: Circle CenterX=318.073 CenterY=120.221 CenterZ=0 NormalX=0 NormalY=0 NormalZ=1 AngleXU=0 Radius=1
    g232: BSplineCurve PolesCount=3 KnotsCount=2 Degree=2 IsPeriodic=0
    g233: GeomPoint X=322.073 Y=124.221 Z=0
    g234: GeomPoint X=318.073 Y=120.221 Z=0
    g235: Circle CenterX=322.073 CenterY=105.865 CenterZ=0 NormalX=0 NormalY=0 NormalZ=1 AngleXU=0 Radius=1
    g236: Circle CenterX=318.073 CenterY=105.865 CenterZ=0 NormalX=0 NormalY=0 NormalZ=1 AngleXU=0 Radius=1
    g237: Circle CenterX=318.073 CenterY=109.865 CenterZ=0 NormalX=0 NormalY=0 NormalZ=1 AngleXU=0 Radius=1
    g238: BSplineCurve PolesCount=3 KnotsCount=2 Degree=2 IsPeriodic=0
    g239: GeomPoint X=322.073 Y=105.865 Z=0
    g240: GeomPoint X=318.073 Y=109.865 Z=0
    g241: Circle CenterX=336.157 CenterY=107.779 CenterZ=0 NormalX=0 NormalY=0 NormalZ=1 AngleXU=0 Radius=1
    g242: Circle CenterX=332.651 CenterY=105.853 CenterZ=0 NormalX=0 NormalY=0 NormalZ=1 AngleXU=0 Radius=1
    g243: Circle CenterX=328.643 CenterY=105.865 CenterZ=0 NormalX=0 NormalY=0 NormalZ=1 AngleXU=0 Radius=1
    g244: BSplineCurve PolesCount=3 KnotsCount=2 Degree=2 IsPeriodic=0
    g245: GeomPoint X=336.157 Y=107.779 Z=0
    g246: GeomPoint X=328.643 Y=105.865 Z=0
    g247: LineSegment StartX=322.073 StartY=124.221 StartZ=0 EndX=362.073 EndY=124.221 EndZ=0
    g248: Circle CenterX=371.567 CenterY=-80.8644 CenterZ=0 NormalX=0 NormalY=0 NormalZ=1 AngleXU=0 Radius=1
    g249: Circle CenterX=375.073 CenterY=-82.7896 CenterZ=0 NormalX=0 NormalY=0 NormalZ=1 AngleXU=0 Radius=1
    g250: Circle CenterX=375.073 CenterY=-78.7896 CenterZ=0 NormalX=0 NormalY=0 NormalZ=1 AngleXU=0 Radius=1
    g251: BSplineCurve PolesCount=3 KnotsCount=2 Degree=2 IsPeriodic=0
    g252: GeomPoint X=371.567 Y=-80.8644 Z=0
    g253: GeomPoint X=375.073 Y=-78.7896 Z=0
    g254: Circle CenterX=321.579 CenterY=-53.4075 CenterZ=0 NormalX=0 NormalY=0 NormalZ=1 AngleXU=0 Radius=1
    g255: Circle CenterX=318.073 CenterY=-51.4823 CenterZ=0 NormalX=0 NormalY=0 NormalZ=1 AngleXU=0 Radius=1
    g256: Circle CenterX=318.073 CenterY=-47.4805 CenterZ=0 NormalX=0 NormalY=0 NormalZ=1 AngleXU=0 Radius=1
    g257: BSplineCurve PolesCount=3 KnotsCount=2 Degree=2 IsPeriodic=0
    g258: GeomPoint X=321.579 Y=-53.4075 Z=0
    g259: GeomPoint X=318.073 Y=-47.4805 Z=0
    g260: LineSegment StartX=371.567 StartY=-80.8644 StartZ=0 EndX=321.579 EndY=-53.4075 EndZ=0
    g261: Circle CenterX=321.579 CenterY=-67.3492 CenterZ=0 NormalX=0 NormalY=0 NormalZ=1 AngleXU=0 Radius=1
    g262: Circle CenterX=318.073 CenterY=-65.424 CenterZ=0 NormalX=0 NormalY=0 NormalZ=1 AngleXU=0 Radius=1
    g263: Circle CenterX=318.073 CenterY=-69.424 CenterZ=0 NormalX=0 NormalY=0 NormalZ=1 AngleXU=0 Radius=1
    g264: BSplineCurve PolesCount=3 KnotsCount=2 Degree=2 IsPeriodic=0
    g265: GeomPoint X=321.579 Y=-67.3492 Z=0
    g266: GeomPoint X=318.073 Y=-69.424 Z=0
    g267: Circle CenterX=362.567 CenterY=-89.8542 CenterZ=0 NormalX=0 NormalY=0 NormalZ=1 AngleXU=0 Radius=1
    g268: Circle CenterX=366.073 CenterY=-91.7794 CenterZ=0 NormalX=0 NormalY=0 NormalZ=1 AngleXU=0 Radius=1
    g269: Circle CenterX=362.073 CenterY=-91.7794 CenterZ=0 NormalX=0 NormalY=0 NormalZ=1 AngleXU=0 Radius=1
    g270: BSplineCurve PolesCount=3 KnotsCount=2 Degree=2 IsPeriodic=0
    g271: GeomPoint X=362.567 Y=-89.8542 Z=0
    g272: GeomPoint X=362.073 Y=-91.7794 Z=0
    g273: Circle CenterX=322.073 CenterY=-91.7794 CenterZ=0 NormalX=0 NormalY=0 NormalZ=1 AngleXU=0 Radius=1
    g274: Circle CenterX=318.073 CenterY=-91.7794 CenterZ=0 NormalX=0 NormalY=0 NormalZ=1 AngleXU=0 Radius=1
    g275: Circle CenterX=318.073 CenterY=-87.7794 CenterZ=0 NormalX=0 NormalY=0 NormalZ=1 AngleXU=0 Radius=1
    g276: BSplineCurve PolesCount=3 KnotsCount=2 Degree=2 IsPeriodic=0
    g277: GeomPoint X=322.073 Y=-91.7794 Z=0
    g278: GeomPoint X=318.073 Y=-87.7794 Z=0
    g279: LineSegment StartX=362.567 StartY=-89.8542 StartZ=0 EndX=321.579 EndY=-67.3492 EndZ=0
    g280: LineSegment StartX=318.073 StartY=-69.424 StartZ=0 EndX=318.073 EndY=-87.7794 EndZ=0
    g281: LineSegment StartX=322.073 StartY=-91.7794 StartZ=0 EndX=362.073 EndY=-91.7794 EndZ=0
    g282: Circle CenterX=2.07281 CenterY=124.221 CenterZ=0 NormalX=0 NormalY=0 NormalZ=1 AngleXU=0 Radius=1
    g283: Circle CenterX=1.57905 CenterY=122.295 CenterZ=0 NormalX=0 NormalY=0 NormalZ=1 AngleXU=0 Radius=1
    g284: BSplineCurve PolesCount=3 KnotsCount=2 Degree=2 IsPeriodic=0
    g285: GeomPoint X=2.07281 Y=124.221 Z=0
    g286: GeomPoint X=1.57905 Y=122.295 Z=0
    g287: Circle CenterX=42.0728 CenterY=124.221 CenterZ=0 NormalX=0 NormalY=0 NormalZ=1 AngleXU=0 Radius=1
    g288: Circle CenterX=46.0728 CenterY=124.221 CenterZ=0 NormalX=0 NormalY=0 NormalZ=1 AngleXU=0 Radius=1
    g289: Circle CenterX=46.0728 CenterY=120.221 CenterZ=0 NormalX=0 NormalY=0 NormalZ=1 AngleXU=0 Radius=1
    g290: BSplineCurve PolesCount=3 KnotsCount=2 Degree=2 IsPeriodic=0
    g291: GeomPoint X=42.0728 Y=124.221 Z=0
    g292: GeomPoint X=46.0728 Y=120.221 Z=0
    g293: Circle CenterX=46.0728 CenterY=109.865 CenterZ=0 NormalX=0 NormalY=0 NormalZ=1 AngleXU=0 Radius=1
    g294: Circle CenterX=46.0728 CenterY=105.865 CenterZ=0 NormalX=0 NormalY=0 NormalZ=1 AngleXU=0 Radius=1
    g295: Circle CenterX=42.0728 CenterY=105.865 CenterZ=0 NormalX=0 NormalY=0 NormalZ=1 AngleXU=0 Radius=1
    g296: BSplineCurve PolesCount=3 KnotsCount=2 Degree=2 IsPeriodic=0
    g297: GeomPoint X=46.0728 Y=109.865 Z=0
    g298: GeomPoint X=42.0728 Y=105.865 Z=0
    g299: Circle CenterX=35.5028 CenterY=105.865 CenterZ=0 NormalX=0 NormalY=0 NormalZ=1 AngleXU=0 Radius=1
    g300: Circle CenterX=31.5028 CenterY=105.865 CenterZ=0 NormalX=0 NormalY=0 NormalZ=1 AngleXU=0 Radius=1
    g301: Circle CenterX=27.9965 CenterY=107.79 CenterZ=0 NormalX=0 NormalY=0 NormalZ=1 AngleXU=0 Radius=1
    g302: BSplineCurve PolesCount=3 KnotsCount=2 Degree=2 IsPeriodic=0
    g303: GeomPoint X=35.5028 Y=105.865 Z=0
    g304: GeomPoint X=27.9965 Y=107.79 Z=0
    g305: LineSegment StartX=2.07281 StartY=124.221 StartZ=0 EndX=42.0728 EndY=124.221 EndZ=0
    g306: LineSegment StartX=46.0728 StartY=120.221 StartZ=0 EndX=46.0728 EndY=109.865 EndZ=0
    g307: LineSegment StartX=42.0728 StartY=105.865 StartZ=0 EndX=35.5028 EndY=105.865 EndZ=0
    g308: LineSegment StartX=27.9965 StartY=107.79 StartZ=0 EndX=1.57905 EndY=122.295 EndZ=0
    g309: Circle CenterX=42.5666 CenterY=-67.3492 CenterZ=0 NormalX=0 NormalY=0 NormalZ=1 AngleXU=0 Radius=1
    g310: Circle CenterX=46.0728 CenterY=-65.424 CenterZ=0 NormalX=0 NormalY=0 NormalZ=1 AngleXU=0 Radius=1
    g311: Circle CenterX=46.0728 CenterY=-69.424 CenterZ=0 NormalX=0 NormalY=0 NormalZ=1 AngleXU=0 Radius=1
    g312: BSplineCurve PolesCount=3 KnotsCount=2 Degree=2 IsPeriodic=0
    g313: GeomPoint X=42.5666 Y=-67.3492 Z=0
    g314: GeomPoint X=46.0728 Y=-69.424 Z=0
    g315: Circle CenterX=46.0728 CenterY=-87.7794 CenterZ=0 NormalX=0 NormalY=0 NormalZ=1 AngleXU=0 Radius=1
    g316: Circle CenterX=46.0728 CenterY=-91.7794 CenterZ=0 NormalX=0 NormalY=0 NormalZ=1 AngleXU=0 Radius=1
    g317: Circle CenterX=42.0728 CenterY=-91.7794 CenterZ=0 NormalX=0 NormalY=0 NormalZ=1 AngleXU=0 Radius=1
    g318: BSplineCurve PolesCount=3 KnotsCount=2 Degree=2 IsPeriodic=0
    g319: GeomPoint X=46.0728 Y=-87.7794 Z=0
    g320: GeomPoint X=42.0728 Y=-91.7794 Z=0
    g321: Circle CenterX=2.07281 CenterY=-91.7794 CenterZ=0 NormalX=0 NormalY=0 NormalZ=1 AngleXU=0 Radius=1
    g322: Circle CenterX=-1.92719 CenterY=-91.7794 CenterZ=0 NormalX=0 NormalY=0 NormalZ=1 AngleXU=0 Radius=1
    g323: Circle CenterX=1.57905 CenterY=-89.8542 CenterZ=0 NormalX=0 NormalY=0 NormalZ=1 AngleXU=0 Radius=1
    g324: BSplineCurve PolesCount=3 KnotsCount=2 Degree=2 IsPeriodic=0
    g325: GeomPoint X=2.07281 Y=-91.7794 Z=0
    g326: GeomPoint X=1.57905 Y=-89.8542 Z=0
    g327: LineSegment StartX=2.07281 StartY=-91.7794 StartZ=0 EndX=42.0728 EndY=-91.7794 EndZ=0
    g328: LineSegment StartX=46.0728 StartY=-87.7794 StartZ=0 EndX=46.0728 EndY=-69.424 EndZ=0
    g329: LineSegment StartX=42.5666 StartY=-67.3492 StartZ=0 EndX=1.57905 EndY=-89.8542 EndZ=0
    g330: Circle CenterX=322.073 CenterY=76.4095 CenterZ=0 NormalX=0 NormalY=0 NormalZ=1 AngleXU=0 Radius=4
    g331: BSplineCurve PolesCount=3 KnotsCount=2 Degree=2 IsPeriodic=0
    g332: GeomPoint X=318.073 Y=72.4095 Z=0
    g333: GeomPoint X=322.073 Y=76.4095 Z=0
    g334: Circle CenterX=375.073 CenterY=72.4095 CenterZ=0 NormalX=0 NormalY=0 NormalZ=1 AngleXU=0 Radius=1
    g335: Circle CenterX=375.073 CenterY=76.4095 CenterZ=0 NormalX=0 NormalY=0 NormalZ=1 AngleXU=0 Radius=1
    g336: Circle CenterX=371.073 CenterY=76.4095 CenterZ=0 NormalX=0 NormalY=0 NormalZ=1 AngleXU=0 Radius=1
    g337: BSplineCurve PolesCount=3 KnotsCount=2 Degree=2 IsPeriodic=0
    g338: GeomPoint X=375.073 Y=72.4095 Z=0
    g339: GeomPoint X=371.073 Y=76.4095 Z=0
    g340: LineSegment StartX=322.073 StartY=76.4095 StartZ=0 EndX=371.073 EndY=76.4095 EndZ=0
    g341: LineSegment StartX=318.073 StartY=72.4095 StartZ=0 EndX=318.073 EndY=-47.4805 EndZ=0
    g342: LineSegment StartX=375.073 StartY=72.4095 StartZ=0 EndX=375.073 EndY=-78.7896 EndZ=0
    g343: ArcOfCircle CenterX=-26.9272 CenterY=22.1087 CenterZ=0 NormalX=0 NormalY=0 NormalZ=1 AngleXU=0 Radius=4 StartAngle=5e-16 EndAngle=3.14159
    g344: LineSegment StartX=-22.9272 StartY=22.1087 StartZ=0 EndX=-18.9272 EndY=-83.7794 EndZ=0
    g345: LineSegment StartX=-34.9272 StartY=-83.7794 StartZ=0 EndX=-30.9272 EndY=22.1087 EndZ=0
    g346: ArcOfCircle CenterX=391.073 CenterY=22.1087 CenterZ=0 NormalX=0 NormalY=0 NormalZ=1 AngleXU=0 Radius=4 StartAngle=0 EndAngle=3.14159
    g347: LineSegment StartX=387.073 StartY=22.1087 StartZ=0 EndX=383.073 EndY=-83.7794 EndZ=0
    g348: LineSegment StartX=395.073 StartY=22.1087 StartZ=0 EndX=399.073 EndY=-83.7794 EndZ=0
    g349: LineSegment StartX=-10.9272 StartY=76.4095 StartZ=0 EndX=-6.92718 EndY=76.4095 EndZ=0
    g350: LineSegment StartX=-10.9272 StartY=76.4095 StartZ=0 EndX=-10.9272 EndY=72.4095 EndZ=0
    g351: LineSegment StartX=46.0728 StartY=76.4095 StartZ=0 EndX=42.0728 EndY=76.4095 EndZ=0
    g352: LineSegment StartX=46.0728 StartY=76.4095 StartZ=0 EndX=46.0728 EndY=72.4095 EndZ=0
    g353: LineSegment StartX=46.0728 StartY=-51.4823 StartZ=0 EndX=46.0728 EndY=-47.4823 EndZ=0
    g354: LineSegment StartX=46.0728 StartY=-51.4823 StartZ=0 EndX=42.5666 EndY=-53.4075 EndZ=0
    g355: LineSegment StartX=-10.9272 StartY=-82.7794 StartZ=0 EndX=-7.42095 EndY=-80.8542 EndZ=0
    g356: LineSegment StartX=-10.9272 StartY=-82.7794 StartZ=0 EndX=-10.9272 EndY=-78.7794 EndZ=0
  constraints (597):
    c: Coincident(g0,g2)
    c: Block(g0)
    c: Block(g1)
    c: Vertical(g3)
    c: Vertical(g4)
    c: Block(g4)
    c: Block(g3)
    c: Weight(g7) = 1
    c: Equal(g7,g8)
    c: Equal(g7,g9)
    c: InternalAlignment(g7,g10)
    c: InternalAlignment(g8,g10)
    c: InternalAlignment(g9,g10)
    c: InternalAlignment(g11,g10)
    c: InternalAlignment(g12,g10)
    c: Weight(g13) = 1
    c: Equal(g13,g14)
    c: Equal(g13,g15)
    c: InternalAlignment(g13,g16)
    c: InternalAlignment(g14,g16)
    c: InternalAlignment(g15,g16)
    c: InternalAlignment(g17,g16)
    c: InternalAlignment(g18,g16)
    c: Block(g16)
    c: Block(g10)
    c: Weight(g19) = 1
    c: Equal(g19,g20)
    c: Equal(g19,g21)
    c: InternalAlignment(g19,g22)
    c: InternalAlignment(g20,g22)
    c: InternalAlignment(g21,g22)
    c: InternalAlignment(g23,g22)
    c: InternalAlignment(g24,g22)
    c: Weight(g25) = 1
    c: Equal(g25,g26)
    c: Equal(g25,g27)
    c: InternalAlignment(g25,g28)
    c: InternalAlignment(g26,g28)
    c: InternalAlignment(g27,g28)
    c: InternalAlignment(g29,g28)
    c: InternalAlignment(g30,g28)
    c: Block(g28)
    c: Block(g22)
    c: Weight(g31) = 1
    c: Equal(g31,g32)
    c: Equal(g31,g33)
    c: InternalAlignment(g31,g34)
    c: InternalAlignment(g32,g34)
    c: InternalAlignment(g33,g34)
    c: InternalAlignment(g35,g34)
    c: InternalAlignment(g36,g34)
    c: Weight(g37) = 1
    c: Equal(g37,g38)
    c: Equal(g37,g39)
    c: InternalAlignment(g37,g40)
    c: InternalAlignment(g38,g40)
    c: InternalAlignment(g39,g40)
    c: InternalAlignment(g41,g40)
    c: InternalAlignment(g42,g40)
    c: Block(g34)
    c: Block(g40)
    c: Coincident(g43,g4)
    c: Coincident(g43,g3)
    c: Horizontal(g43)
    c: Distance(g43) = 450
    c: Coincident(g44,g4)
    c: Coincident(g44,g3)
    c: Horizontal(g44)
    c: Horizontal(g45)
    c: Coincident(g2,g45)
    c: Block(g45)
    c: Coincident(g1,g45)
    c: Weight(g46) = 1
    c: Equal(g46,g47)
    c: Equal(g46,g48)
    c: InternalAlignment(g46,g49)
    c: InternalAlignment(g47,g49)
    c: InternalAlignment(g48,g49)
    c: InternalAlignment(g50,g49)
    c: InternalAlignment(g51,g49)
    c: Block(g49)
    c: Weight(g52) = 1
    c: Equal(g52,g53)
    c: Equal(g52,g54)
    c: InternalAlignment(g52,g55)
    c: InternalAlignment(g53,g55)
    c: InternalAlignment(g54,g55)
    c: InternalAlignment(g56,g55)
    c: InternalAlignment(g57,g55)
    c: Block(g55)
    c: Weight(g58) = 1
    c: Equal(g58,g59)
    c: Equal(g58,g60)
    c: InternalAlignment(g58,g61)
    c: InternalAlignment(g59,g61)
    c: InternalAlignment(g60,g61)
    c: InternalAlignment(g62,g61)
    c: InternalAlignment(g63,g61)
    c: Block(g61)
    c: Weight(g64) = 1
    c: Equal(g64,g65)
    c: Equal(g64,g66)
    c: InternalAlignment(g64,g67)
    c: InternalAlignment(g65,g67)
    c: InternalAlignment(g66,g67)
    c: InternalAlignment(g68,g67)
    c: InternalAlignment(g69,g67)
    c: Block(g67)
    c: Weight(g70) = 1
    c: Equal(g70,g71)
    c: Equal(g70,g72)
    c: InternalAlignment(g70,g73)
    c: InternalAlignment(g71,g73)
    c: InternalAlignment(g72,g73)
    c: InternalAlignment(g74,g73)
    c: InternalAlignment(g75,g73)
    c: Weight(g76) = 1
    c: Equal(g76,g77)
    c: Equal(g76,g78)
    c: InternalAlignment(g76,g79)
    c: InternalAlignment(g77,g79)
    c: InternalAlignment(g78,g79)
    c: InternalAlignment(g80,g79)
    c: InternalAlignment(g81,g79)
    c: Block(g73)
    c: Block(g79)
    c: Coincident(g82,g73)
    c: Coincident(g82,g79)
    c: Vertical(g82)
    c: Coincident(g83,g73)
    c: Coincident(g83,g55)
    c: Coincident(g84,g55)
    c: Coincident(g84,g79)
    c: Weight(g85) = 1
    c: Equal(g85,g86)
    c: Equal(g85,g87)
    c: InternalAlignment(g85,g88)
    c: InternalAlignment(g86,g88)
    c: InternalAlignment(g87,g88)
    c: InternalAlignment(g89,g88)
    c: InternalAlignment(g90,g88)
    c: Weight(g91) = 1
    c: Equal(g91,g92)
    c: Equal(g91,g93)
    c: InternalAlignment(g91,g94)
    c: InternalAlignment(g92,g94)
    c: InternalAlignment(g93,g94)
    c: InternalAlignment(g95,g94)
    c: InternalAlignment(g96,g94)
    c: Block(g88)
    c: Block(g94)
    c: Coincident(g97,g88)
    c: Coincident(g97,g94)
    c: Vertical(g97)
    c: Coincident(g98,g88)
    c: Coincident(g98,g49)
    c: Coincident(g99,g49)
    c: Coincident(g99,g94)
    c: Weight(g100) = 1
    c: Equal(g100,g101)
    c: Equal(g100,g102)
    c: InternalAlignment(g100,g103)
    c: InternalAlignment(g101,g103)
    c: InternalAlignment(g102,g103)
    c: InternalAlignment(g104,g103)
    c: InternalAlignment(g105,g103)
    c: Weight(g106) = 1
    c: Equal(g106,g107)
    c: Equal(g106,g108)
    c: InternalAlignment(g106,g109)
    c: InternalAlignment(g107,g109)
    c: InternalAlignment(g108,g109)
    c: InternalAlignment(g110,g109)
    c: InternalAlignment(g111,g109)
    c: Block(g103)
    c: Block(g109)
    c: Coincident(g112,g103)
    c: Coincident(g112,g109)
    c: Vertical(g112)
    c: Coincident(g113,g109)
    c: Coincident(g113,g67)
    c: Coincident(g114,g67)
    c: Coincident(g114,g103)
    c: Weight(g115) = 1
    c: Equal(g115,g116)
    c: Equal(g115,g117)
    c: InternalAlignment(g115,g118)
    c: InternalAlignment(g116,g118)
    c: InternalAlignment(g117,g118)
    c: InternalAlignment(g119,g118)
    c: InternalAlignment(g120,g118)
    c: Weight(g121) = 1
    c: Equal(g121,g122)
    c: Equal(g121,g123)
    c: InternalAlignment(g121,g124)
    c: InternalAlignment(g122,g124)
    c: InternalAlignment(g123,g124)
    c: InternalAlignment(g125,g124)
    c: InternalAlignment(g126,g124)
    c: Block(g118)
    c: Block(g124)
    c: Coincident(g127,g118)
    c: Coincident(g127,g124)
    c: Vertical(g127)
    c: Coincident(g128,g124)
    c: Coincident(g128,g61)
    c: Coincident(g129,g61)
    c: Coincident(g129,g118)
    c: Weight(g130) = 1
    c: Equal(g130,g131)
    c: Equal(g130,g132)
    c: InternalAlignment(g130,g133)
    c: InternalAlignment(g131,g133)
    c: InternalAlignment(g132,g133)
    c: InternalAlignment(g134,g133)
    c: InternalAlignment(g135,g133)
    c: Weight(g136) = 1
    c: Equal(g136,g137)
    c: Equal(g136,g138)
    c: InternalAlignment(g136,g139)
    c: InternalAlignment(g137,g139)
    c: InternalAlignment(g138,g139)
    c: InternalAlignment(g140,g139)
    c: InternalAlignment(g141,g139)
    c: Weight(g142) = 1
    c: Equal(g142,g143)
    c: Equal(g142,g144)
    c: InternalAlignment(g142,g145)
    c: InternalAlignment(g143,g145)
    c: InternalAlignment(g144,g145)
    c: InternalAlignment(g146,g145)
    c: InternalAlignment(g147,g145)
    c: Weight(g148) = 1
    c: Equal(g148,g149)
    c: Equal(g148,g150)
    c: InternalAlignment(g148,g151)
    c: InternalAlignment(g149,g151)
    c: InternalAlignment(g150,g151)
    c: InternalAlignment(g152,g151)
    c: InternalAlignment(g153,g151)
    c: Block(g151)
    c: Block(g145)
    c: Block(g139)
    c: Block(g133)
    c: Coincident(g154,g28)
    c: Coincident(g154,g151)
    c: Coincident(g155,g151)
    c: Coincident(g155,g145)
    c: Horizontal(g155)
    c: Coincident(g156,g145)
    c: Coincident(g156,g28)
    c: Vertical(g156)
    c: Coincident(g157,g22)
    c: Coincident(g157,g139)
    c: Vertical(g157)
    c: Coincident(g158,g139)
    c: Coincident(g158,g133)
    c: Horizontal(g158)
    c: Coincident(g159,g133)
    c: Coincident(g159,g22)
    c: Weight(g160) = 1
    c: Equal(g160,g161)
    c: Equal(g160,g162)
    c: InternalAlignment(g160,g163)
    c: InternalAlignment(g161,g163)
    c: InternalAlignment(g162,g163)
    c: InternalAlignment(g164,g163)
    c: InternalAlignment(g165,g163)
    c: Weight(g166) = 1
    c: Equal(g166,g167)
    c: Equal(g166,g168)
    c: InternalAlignment(g166,g169)
    c: InternalAlignment(g167,g169)
    c: InternalAlignment(g168,g169)
    c: InternalAlignment(g170,g169)
    c: InternalAlignment(g171,g169)
    c: Weight(g172) = 1
    c: Equal(g172,g173)
    c: Equal(g172,g174)
    c: InternalAlignment(g172,g175)
    c: InternalAlignment(g173,g175)
    c: InternalAlignment(g174,g175)
    c: InternalAlignment(g176,g175)
    c: InternalAlignment(g177,g175)
    c: Weight(g178) = 1
    c: Equal(g178,g179)
    c: Equal(g178,g180)
    c: InternalAlignment(g178,g181)
    c: InternalAlignment(g179,g181)
    c: InternalAlignment(g180,g181)
    c: InternalAlignment(g182,g181)
    c: InternalAlignment(g183,g181)
    c: Block(g181)
    c: Block(g175)
    c: Block(g169)
    c: Block(g163)
    c: Coincident(g184,g181)
    c: Coincident(g184,g175)
    c: Horizontal(g184)
    c: Coincident(g185,g175)
    c: Coincident(g185,g10)
    c: Vertical(g185)
    c: Coincident(g186,g16)
    c: Coincident(g186,g169)
    c: Vertical(g186)
    c: Coincident(g187,g169)
    c: Coincident(g187,g163)
    c: Horizontal(g187)
    c: Coincident(g188,g163)
    c: Coincident(g188,g16)
    c: Coincident(g189,g10)
    c: Weight(g190) = 1
    c: Equal(g190,g191)
    c: Equal(g190,g192)
    c: InternalAlignment(g190,g193)
    c: InternalAlignment(g191,g193)
    c: InternalAlignment(g192,g193)
    c: InternalAlignment(g194,g193)
    c: InternalAlignment(g195,g193)
    c: Weight(g196) = 1
    c: Equal(g196,g197)
    c: Equal(g196,g198)
    c: InternalAlignment(g196,g199)
    c: InternalAlignment(g197,g199)
    c: InternalAlignment(g198,g199)
    c: InternalAlignment(g200,g199)
    c: InternalAlignment(g201,g199)
    c: Block(g199)
    c: Block(g193)
    c: Coincident(g202,g199)
    c: Coincident(g202,g34)
    c: Coincident(g203,g34)
    c: Coincident(g203,g193)
    c: Coincident(g204,g193)
    c: Coincident(g204,g199)
    c: Vertical(g204)
    c: Weight(g205) = 1
    c: Equal(g205,g206)
    c: Equal(g205,g207)
    c: InternalAlignment(g205,g208)
    c: InternalAlignment(g206,g208)
    c: InternalAlignment(g207,g208)
    c: InternalAlignment(g209,g208)
    c: InternalAlignment(g210,g208)
    c: Weight(g211) = 1
    c: Equal(g211,g212)
    c: Equal(g211,g213)
    c: InternalAlignment(g211,g214)
    c: InternalAlignment(g212,g214)
    c: InternalAlignment(g213,g214)
    c: InternalAlignment(g215,g214)
    c: InternalAlignment(g216,g214)
    c: Block(g214)
    c: Block(g208)
    c: Coincident(g217,g208)
    c: Coincident(g217,g40)
    c: Coincident(g218,g40)
    c: Coincident(g218,g214)
    c: Coincident(g219,g214)
    c: Coincident(g219,g208)
    c: Vertical(g219)
    c: Horizontal(g220)
    c: Block(g220)
    c: Vertical(g221)
    c: Block(g221)
    c: Block(g222)
    c: Weight(g223) = 1
    c: Equal(g223,g224)
    c: Equal(g223,g225)
    c: InternalAlignment(g223,g226)
    c: InternalAlignment(g224,g226)
    c: InternalAlignment(g225,g226)
    c: InternalAlignment(g227,g226)
    c: InternalAlignment(g228,g226)
    c: Weight(g229) = 1
    c: Equal(g229,g230)
    c: Equal(g229,g231)
    c: InternalAlignment(g229,g232)
    c: InternalAlignment(g230,g232)
    c: InternalAlignment(g231,g232)
    c: InternalAlignment(g233,g232)
    c: InternalAlignment(g234,g232)
    c: Weight(g235) = 1
    c: Equal(g235,g236)
    c: Equal(g235,g237)
    c: InternalAlignment(g235,g238)
    c: InternalAlignment(g236,g238)
    c: InternalAlignment(g237,g238)
    c: InternalAlignment(g239,g238)
    c: InternalAlignment(g240,g238)
    c: Weight(g241) = 1
    c: Equal(g241,g242)
    c: Equal(g241,g243)
    c: InternalAlignment(g241,g244)
    c: InternalAlignment(g242,g244)
    c: InternalAlignment(g243,g244)
    c: InternalAlignment(g245,g244)
    c: InternalAlignment(g246,g244)
    c: Block(g226)
    c: Block(g232)
    c: Block(g238)
    c: Block(g244)
    c: Coincident(g247,g232)
    c: Coincident(g247,g226)
    c: Horizontal(g247)
    c: Block(g189)
    c: Weight(g248) = 1
    c: Equal(g248,g249)
    c: Equal(g248,g250)
    c: InternalAlignment(g248,g251)
    c: InternalAlignment(g249,g251)
    c: InternalAlignment(g250,g251)
    c: InternalAlignment(g252,g251)
    c: InternalAlignment(g253,g251)
    c: Weight(g254) = 1
    c: Equal(g254,g255)
    c: Equal(g254,g256)
    c: InternalAlignment(g254,g257)
    c: InternalAlignment(g255,g257)
    c: InternalAlignment(g256,g257)
    c: InternalAlignment(g258,g257)
    c: InternalAlignment(g259,g257)
    c: Block(g251)
    c: Block(g257)
    c: Coincident(g260,g251)
    c: Coincident(g260,g257)
    c: Weight(g261) = 1
    c: Equal(g261,g262)
    c: Equal(g261,g263)
    c: InternalAlignment(g261,g264)
    c: InternalAlignment(g262,g264)
    c: InternalAlignment(g263,g264)
    c: InternalAlignment(g265,g264)
    c: InternalAlignment(g266,g264)
    c: Weight(g267) = 1
    c: Equal(g267,g268)
    c: Equal(g267,g269)
    c: InternalAlignment(g267,g270)
    c: InternalAlignment(g268,g270)
    c: InternalAlignment(g269,g270)
    c: InternalAlignment(g271,g270)
    c: InternalAlignment(g272,g270)
    c: Weight(g273) = 1
    c: Equal(g273,g274)
    c: Equal(g273,g275)
    c: InternalAlignment(g273,g276)
    c: InternalAlignment(g274,g276)
    c: InternalAlignment(g275,g276)
    c: InternalAlignment(g277,g276)
    c: InternalAlignment(g278,g276)
    c: Block(g276)
    c: Block(g270)
    c: Block(g264)
    c: Coincident(g279,g270)
    c: Coincident(g279,g264)
    c: Coincident(g280,g264)
    c: Coincident(g280,g276)
    c: Vertical(g280)
    c: Coincident(g281,g276)
    c: Coincident(g281,g270)
    c: Horizontal(g281)
    c: Weight(g282) = 1
    c: Equal(g282,g283)
    c: InternalAlignment(g282,g284)
    c: InternalAlignment(g283,g284)
    c: InternalAlignment(g285,g284)
    c: InternalAlignment(g286,g284)
    c: Weight(g287) = 1
    c: InternalAlignment(g288,g290)
    c: InternalAlignment(g289,g290)
    c: InternalAlignment(g291,g290)
    c: InternalAlignment(g292,g290)
    c: Weight(g293) = 1
    c: Equal(g293,g294)
    c: Equal(g293,g295)
    c: InternalAlignment(g293,g296)
    c: InternalAlignment(g294,g296)
    c: InternalAlignment(g295,g296)
    c: InternalAlignment(g297,g296)
    c: InternalAlignment(g298,g296)
    c: Equal(g299,g300)
    c: Equal(g299,g301)
    c: InternalAlignment(g299,g302)
    c: InternalAlignment(g300,g302)
    c: InternalAlignment(g301,g302)
    c: InternalAlignment(g303,g302)
    c: InternalAlignment(g304,g302)
    c: Block(g290)
    c: Block(g296)
    c: Block(g302)
    c: Block(g284)
    c: Coincident(g305,g284)
    c: Coincident(g305,g290)
    c: Horizontal(g305)
    c: Coincident(g306,g290)
    c: Coincident(g306,g296)
    c: Vertical(g306)
    c: Coincident(g307,g296)
    c: Coincident(g307,g302)
    c: Horizontal(g307)
    c: Coincident(g308,g302)
    c: Coincident(g308,g284)
    c: Weight(g309) = 1
    c: Equal(g309,g310)
    c: Equal(g309,g311)
    c: InternalAlignment(g309,g312)
    c: InternalAlignment(g310,g312)
    c: InternalAlignment(g311,g312)
    c: InternalAlignment(g313,g312)
    c: InternalAlignment(g314,g312)
    c: Weight(g315) = 1
    c: Equal(g315,g316)
    c: Equal(g315,g317)
    c: InternalAlignment(g315,g318)
    c: InternalAlignment(g316,g318)
    c: InternalAlignment(g317,g318)
    c: InternalAlignment(g319,g318)
    c: InternalAlignment(g320,g318)
    c: Weight(g321) = 1
    c: Equal(g321,g322)
    c: Equal(g321,g323)
    c: InternalAlignment(g321,g324)
    c: InternalAlignment(g322,g324)
    c: InternalAlignment(g323,g324)
    c: InternalAlignment(g325,g324)
    c: InternalAlignment(g326,g324)
    c: Block(g324)
    c: Block(g318)
    c: Block(g312)
    c: Coincident(g327,g324)
    c: Coincident(g327,g318)
    c: Horizontal(g327)
    c: Coincident(g328,g318)
    c: Coincident(g328,g312)
    c: Vertical(g328)
    c: Coincident(g329,g312)
    c: Coincident(g329,g324)
    c: InternalAlignment(g330,g331)
    c: InternalAlignment(g332,g331)
    c: InternalAlignment(g333,g331)
    c: Block(g331)
    c: Equal(g334,g335)
    c: Equal(g334,g336)
    c: InternalAlignment(g334,g337)
    c: InternalAlignment(g335,g337)
    c: InternalAlignment(g336,g337)
    c: InternalAlignment(g338,g337)
    c: InternalAlignment(g339,g337)
    c: Block(g337)
    c: Coincident(g340,g331)
    c: Horizontal(g340)
    c: Block(g340)
    c: Coincident(g341,g331)
    c: Coincident(g341,g257)
    c: Vertical(g341)
    c: Coincident(g342,g337)
    c: Coincident(g342,g251)
    c: Vertical(g342)
    c: Block(g343)
    c: Block(g5)
    c: Distance(g341) = 119.89
    c: Coincident(g344,g343)
    c: Coincident(g344,g5)
    c: Coincident(g345,g5)
    c: Coincident(g345,g343)
    c: Block(g6)
    c: Block(g346)
    c: Coincident(g347,g346)
    c: Coincident(g347,g6)
    c: Coincident(g348,g346)
    c: Coincident(g348,g6)
    c: Block(g348)
    c: Block(g347)
    c: Horizontal(g349)
    c: Vertical(g350)
    c: Horizontal(g351)
    c: Vertical(g352)
    c: Vertical(g353)
    c: Vertical(g356)
    c: Parallel(g0,g355)
    c: Parallel(g354,g0)
    c: Distance(g354) = 4
    c: Distance(g353) = 4
    c: Distance(g355) = 4
    c: Distance(g356) = 4
    c: Distance(g349) = 4
    c: Distance(g350) = 4
    c: Distance(g351) = 4
    c: Distance(g352) = 4
    c: Coincident(g349,g1)
    c: Coincident(g350,g1)
    c: Coincident(g352,g2)
    c: Coincident(g351,g2)
    c: Coincident(g353,g0)
    c: Coincident(g354,g0)
    c: Coincident(g355,g0)
    c: Coincident(g356,g0)
